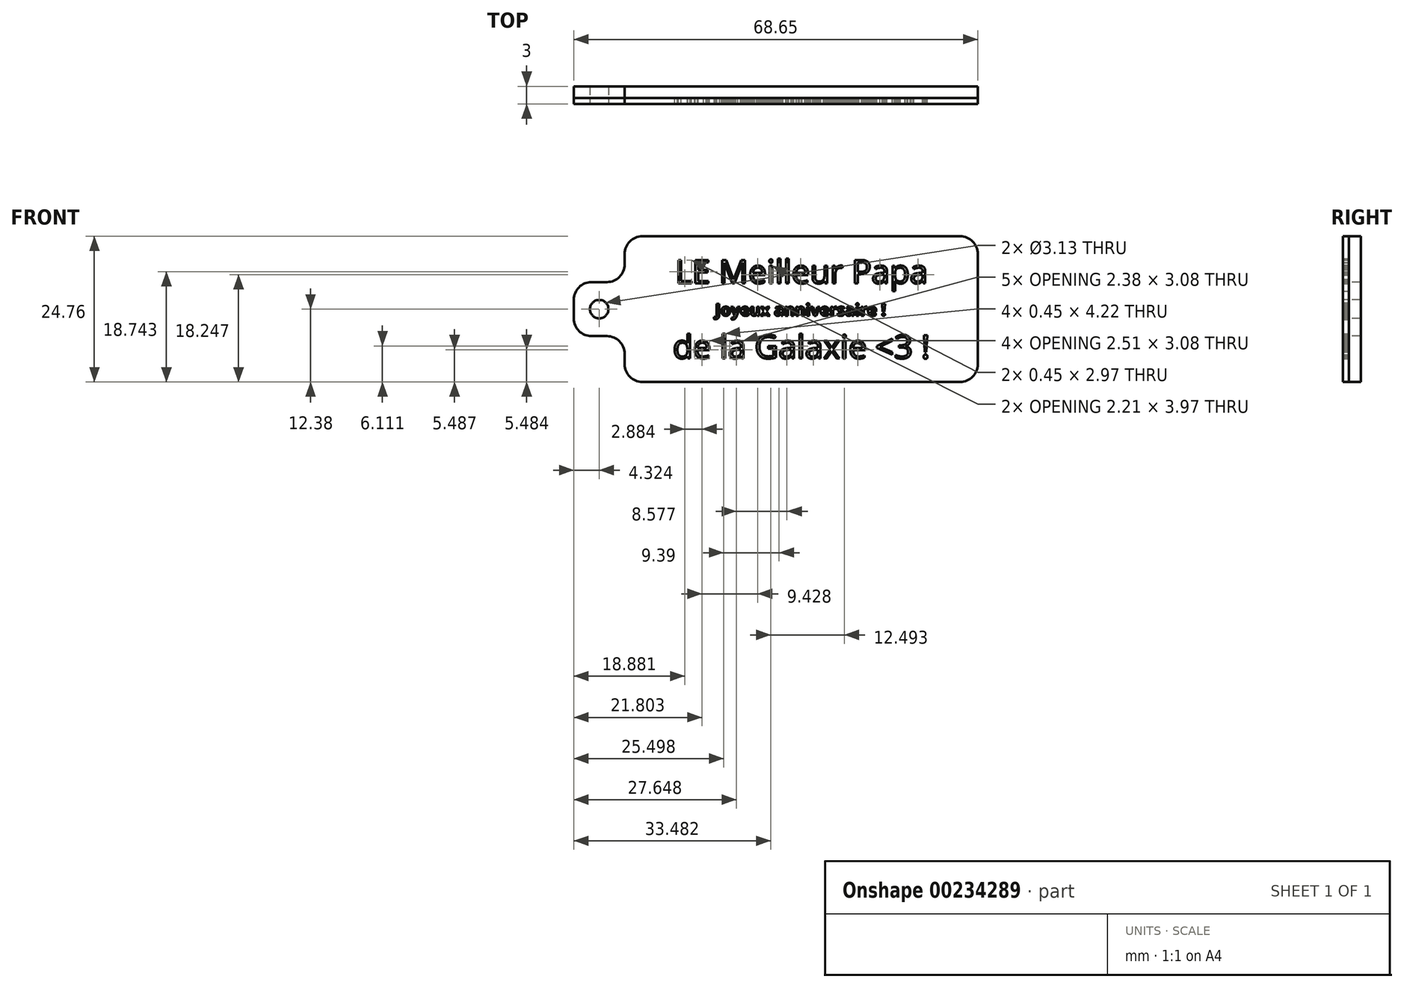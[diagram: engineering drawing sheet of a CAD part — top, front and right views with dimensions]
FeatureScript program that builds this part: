
annotation { "Feature Type Name" : "Feature", "Feature Type Description" : "" }
export const myFeature = defineFeature(function(context is Context, id is Id, definition is map)
    precondition{}
    {
        {
            var Q0;
            Q0=qCreatedBy(makeId("Front.planeOp"),FACE);
            var sketch = newSketch(context, id + "F0", { "sketchPlane" : qUnion([Q0])});
            skLineSegment(sketch, "E0.bottom", {"start": v(30, -12.38) * mm, "end": v(-30, -12.38) * mm});
            skLineSegment(sketch, "E0.top", {"start": v(30, 12.38) * mm, "end": v(-30, 12.38) * mm});
            skLineSegment(sketch, "E0.left", {"start": v(30, -12.38) * mm, "end": v(30, 12.38) * mm});
            skLineSegment(sketch, "E0.right", {"start": v(-30, -12.38) * mm, "end": v(-30, 12.38) * mm});
            skPoint(sketch, "E0.middle", {"position": v(0, 0) * mm});
            skText(sketch, "E1", { "text": "LE Meilleur Papa", "fontName": "OpenSans-Regular.ttf"});
            skLineSegment(sketch, "E2", {"start": v(0, 12.38) * mm, "end": v(0, 0) * mm, "construction": true});
            skText(sketch, "E3", { "text": "de la Galaxie <3 !", "fontName": "OpenSans-Regular.ttf"});
            skLineSegment(sketch, "E4.bottom", {"start": v(-30, -4.6) * mm, "end": v(-38.65, -4.6) * mm});
            skLineSegment(sketch, "E4.top", {"start": v(-30, 4.6) * mm, "end": v(-38.65, 4.6) * mm});
            skLineSegment(sketch, "E4.left", {"start": v(-30, -4.6) * mm, "end": v(-30, 4.6) * mm});
            skLineSegment(sketch, "E4.right", {"start": v(-38.65, -4.6) * mm, "end": v(-38.65, 4.6) * mm});
            skPoint(sketch, "E4.middle", {"position": v(-34.33, 0) * mm});
            skPoint(sketch, "E4.middle.positionSnap0", {"position": v(-30, 0) * mm});
            skPoint(sketch, "E4.centerSnap0", {"position": v(-30, 0) * mm});
            const initialGuessF0  = {"E1": [-0.02142, 0.00438, 1, 0, 0.004], "E3": [-0.02182, -0.00838, 1, 0, 0.004]};
            skSetInitialGuess(sketch, initialGuessF0);
            skSolve(sketch);
        }
        {
            var Q0;
            Q0 = qSketchRegion(id + "F0", true);
            var Q1;
            Q1=makeQuery(id+"F0.imprint","IMPRINT",FACE,{"disambiguationData":[TD([[makeQuery(id+"F0.imprint","IMPRINT",EDGE,{"derivedFrom":sQuery(id+"F0.wireOp",EDGE,"E1.sketch_text.stroke-50")}),1.0]])]});
            var Q2;
            Q2=makeQuery(id+"F0.imprint","IMPRINT",FACE,{"disambiguationData":[TD([[makeQuery(id+"F0.imprint","IMPRINT",EDGE,{"derivedFrom":sQuery(id+"F0.wireOp",EDGE,"E1.sketch_text.stroke-89")}),1.0]])]});
            var Q3;
            Q3=makeQuery(id+"F0.imprint","IMPRINT",FACE,{"disambiguationData":[TD([[makeQuery(id+"F0.imprint","IMPRINT",EDGE,{"derivedFrom":sQuery(id+"F0.wireOp",EDGE,"E1.sketch_text.stroke-132")}),1.0]])]});
            var Q4;
            Q4=makeQuery(id+"F0.imprint","IMPRINT",FACE,{"disambiguationData":[TD([[makeQuery(id+"F0.imprint","IMPRINT",EDGE,{"derivedFrom":sQuery(id+"F0.wireOp",EDGE,"E1.sketch_text.stroke-158")}),1.0]])]});
            var Q5;
            Q5=makeQuery(id+"F0.imprint","IMPRINT",FACE,{"disambiguationData":[TD([[makeQuery(id+"F0.imprint","IMPRINT",EDGE,{"derivedFrom":sQuery(id+"F0.wireOp",EDGE,"E1.sketch_text.stroke-182")}),1.0]])]});
            var Q6;
            Q6=makeQuery(id+"F0.imprint","IMPRINT",FACE,{"disambiguationData":[TD([[makeQuery(id+"F0.imprint","IMPRINT",EDGE,{"derivedFrom":sQuery(id+"F0.wireOp",EDGE,"E1.sketch_text.stroke-210")}),1.0]])]});
            var Q7;
            Q7=makeQuery(id+"F0.imprint","IMPRINT",FACE,{"disambiguationData":[TD([[makeQuery(id+"F0.imprint","IMPRINT",EDGE,{"derivedFrom":sQuery(id+"F0.wireOp",EDGE,"E3.sketch_text.stroke-15")}),1.0]])]});
            var Q8;
            Q8=makeQuery(id+"F0.imprint","IMPRINT",FACE,{"disambiguationData":[TD([[makeQuery(id+"F0.imprint","IMPRINT",EDGE,{"derivedFrom":sQuery(id+"F0.wireOp",EDGE,"E3.sketch_text.stroke-38")}),1.0]])]});
            var Q9;
            Q9=makeQuery(id+"F0.imprint","IMPRINT",FACE,{"disambiguationData":[TD([[makeQuery(id+"F0.imprint","IMPRINT",EDGE,{"derivedFrom":sQuery(id+"F0.wireOp",EDGE,"E3.sketch_text.stroke-66")}),1.0]])]});
            var Q10;
            Q10=makeQuery(id+"F0.imprint","IMPRINT",FACE,{"disambiguationData":[TD([[makeQuery(id+"F0.imprint","IMPRINT",EDGE,{"derivedFrom":sQuery(id+"F0.wireOp",EDGE,"E3.sketch_text.stroke-113")}),1.0]])]});
            var Q11;
            Q11=makeQuery(id+"F0.imprint","IMPRINT",FACE,{"disambiguationData":[TD([[makeQuery(id+"F0.imprint","IMPRINT",EDGE,{"derivedFrom":sQuery(id+"F0.wireOp",EDGE,"E3.sketch_text.stroke-144")}),1.0]])]});
            var Q12;
            Q12=makeQuery(id+"F0.imprint","IMPRINT",FACE,{"disambiguationData":[TD([[makeQuery(id+"F0.imprint","IMPRINT",EDGE,{"derivedFrom":sQuery(id+"F0.wireOp",EDGE,"E3.sketch_text.stroke-190")}),1.0]])]});
            extrude(context, id + "F1", {"entities" : qUnion([Q0, Q1, Q2, Q3, Q4, Q5, Q6, Q7, Q8, Q9, Q10, Q11, Q12]), "depth" : 1 * mm});
        }
        {
            var Q0;
            Q0=makeQuery(id+"F1.opExtrude","CAP_FACE",FACE,{"disambiguationData":[OSD([sQuery(id+"F0.wireOp",EDGE,"E0.bottom"),sQuery(id+"F0.wireOp",EDGE,"E0.top"),sQuery(id+"F0.wireOp",EDGE,"E0.left"),sQuery(id+"F0.wireOp",EDGE,"E0.right"),sQuery(id+"F0.wireOp",EDGE,"E1.sketch_text.stroke-0"),sQuery(id+"F0.wireOp",EDGE,"E1.sketch_text.stroke-1"),sQuery(id+"F0.wireOp",EDGE,"E1.sketch_text.stroke-2"),sQuery(id+"F0.wireOp",EDGE,"E1.sketch_text.stroke-3"),sQuery(id+"F0.wireOp",EDGE,"E1.sketch_text.stroke-4"),sQuery(id+"F0.wireOp",EDGE,"E1.sketch_text.stroke-5"),sQuery(id+"F0.wireOp",EDGE,"E1.sketch_text.stroke-6"),sQuery(id+"F0.wireOp",EDGE,"E1.sketch_text.stroke-7"),sQuery(id+"F0.wireOp",EDGE,"E1.sketch_text.stroke-8"),sQuery(id+"F0.wireOp",EDGE,"E1.sketch_text.stroke-9"),sQuery(id+"F0.wireOp",EDGE,"E1.sketch_text.stroke-10"),sQuery(id+"F0.wireOp",EDGE,"E1.sketch_text.stroke-11"),sQuery(id+"F0.wireOp",EDGE,"E1.sketch_text.stroke-12"),sQuery(id+"F0.wireOp",EDGE,"E1.sketch_text.stroke-13"),sQuery(id+"F0.wireOp",EDGE,"E1.sketch_text.stroke-14"),sQuery(id+"F0.wireOp",EDGE,"E1.sketch_text.stroke-15"),sQuery(id+"F0.wireOp",EDGE,"E1.sketch_text.stroke-16"),sQuery(id+"F0.wireOp",EDGE,"E1.sketch_text.stroke-17"),sQuery(id+"F0.wireOp",EDGE,"E1.sketch_text.stroke-18"),sQuery(id+"F0.wireOp",EDGE,"E1.sketch_text.stroke-19"),sQuery(id+"F0.wireOp",EDGE,"E1.sketch_text.stroke-20"),sQuery(id+"F0.wireOp",EDGE,"E1.sketch_text.stroke-21"),sQuery(id+"F0.wireOp",EDGE,"E1.sketch_text.stroke-22"),sQuery(id+"F0.wireOp",EDGE,"E1.sketch_text.stroke-23"),sQuery(id+"F0.wireOp",EDGE,"E1.sketch_text.stroke-24"),sQuery(id+"F0.wireOp",EDGE,"E1.sketch_text.stroke-25"),sQuery(id+"F0.wireOp",EDGE,"E1.sketch_text.stroke-26"),sQuery(id+"F0.wireOp",EDGE,"E1.sketch_text.stroke-27"),sQuery(id+"F0.wireOp",EDGE,"E1.sketch_text.stroke-28"),sQuery(id+"F0.wireOp",EDGE,"E1.sketch_text.stroke-29"),sQuery(id+"F0.wireOp",EDGE,"E1.sketch_text.stroke-30"),sQuery(id+"F0.wireOp",EDGE,"E1.sketch_text.stroke-31"),sQuery(id+"F0.wireOp",EDGE,"E1.sketch_text.stroke-32"),sQuery(id+"F0.wireOp",EDGE,"E1.sketch_text.stroke-33"),sQuery(id+"F0.wireOp",EDGE,"E1.sketch_text.stroke-34"),sQuery(id+"F0.wireOp",EDGE,"E1.sketch_text.stroke-35"),sQuery(id+"F0.wireOp",EDGE,"E1.sketch_text.stroke-36"),sQuery(id+"F0.wireOp",EDGE,"E1.sketch_text.stroke-37"),sQuery(id+"F0.wireOp",EDGE,"E1.sketch_text.stroke-38"),sQuery(id+"F0.wireOp",EDGE,"E1.sketch_text.stroke-39"),sQuery(id+"F0.wireOp",EDGE,"E1.sketch_text.stroke-40"),sQuery(id+"F0.wireOp",EDGE,"E1.sketch_text.stroke-41"),sQuery(id+"F0.wireOp",EDGE,"E1.sketch_text.stroke-42"),sQuery(id+"F0.wireOp",EDGE,"E1.sketch_text.stroke-43"),sQuery(id+"F0.wireOp",EDGE,"E1.sketch_text.stroke-44"),sQuery(id+"F0.wireOp",EDGE,"E1.sketch_text.stroke-45"),sQuery(id+"F0.wireOp",EDGE,"E1.sketch_text.stroke-46"),sQuery(id+"F0.wireOp",EDGE,"E1.sketch_text.stroke-47"),sQuery(id+"F0.wireOp",EDGE,"E1.sketch_text.stroke-48"),sQuery(id+"F0.wireOp",EDGE,"E1.sketch_text.stroke-49"),sQuery(id+"F0.wireOp",EDGE,"E1.sketch_text.stroke-55"),sQuery(id+"F0.wireOp",EDGE,"E1.sketch_text.stroke-56"),sQuery(id+"F0.wireOp",EDGE,"E1.sketch_text.stroke-57"),sQuery(id+"F0.wireOp",EDGE,"E1.sketch_text.stroke-58"),sQuery(id+"F0.wireOp",EDGE,"E1.sketch_text.stroke-59"),sQuery(id+"F0.wireOp",EDGE,"E1.sketch_text.stroke-60"),sQuery(id+"F0.wireOp",EDGE,"E1.sketch_text.stroke-61"),sQuery(id+"F0.wireOp",EDGE,"E1.sketch_text.stroke-62"),sQuery(id+"F0.wireOp",EDGE,"E1.sketch_text.stroke-63"),sQuery(id+"F0.wireOp",EDGE,"E1.sketch_text.stroke-64"),sQuery(id+"F0.wireOp",EDGE,"E1.sketch_text.stroke-65"),sQuery(id+"F0.wireOp",EDGE,"E1.sketch_text.stroke-66"),sQuery(id+"F0.wireOp",EDGE,"E1.sketch_text.stroke-67"),sQuery(id+"F0.wireOp",EDGE,"E1.sketch_text.stroke-68"),sQuery(id+"F0.wireOp",EDGE,"E1.sketch_text.stroke-69"),sQuery(id+"F0.wireOp",EDGE,"E1.sketch_text.stroke-70"),sQuery(id+"F0.wireOp",EDGE,"E1.sketch_text.stroke-71"),sQuery(id+"F0.wireOp",EDGE,"E1.sketch_text.stroke-72"),sQuery(id+"F0.wireOp",EDGE,"E1.sketch_text.stroke-73"),sQuery(id+"F0.wireOp",EDGE,"E1.sketch_text.stroke-74"),sQuery(id+"F0.wireOp",EDGE,"E1.sketch_text.stroke-75"),sQuery(id+"F0.wireOp",EDGE,"E1.sketch_text.stroke-76"),sQuery(id+"F0.wireOp",EDGE,"E1.sketch_text.stroke-77"),sQuery(id+"F0.wireOp",EDGE,"E1.sketch_text.stroke-78"),sQuery(id+"F0.wireOp",EDGE,"E1.sketch_text.stroke-79"),sQuery(id+"F0.wireOp",EDGE,"E1.sketch_text.stroke-80"),sQuery(id+"F0.wireOp",EDGE,"E1.sketch_text.stroke-81"),sQuery(id+"F0.wireOp",EDGE,"E1.sketch_text.stroke-82"),sQuery(id+"F0.wireOp",EDGE,"E1.sketch_text.stroke-83"),sQuery(id+"F0.wireOp",EDGE,"E1.sketch_text.stroke-84"),sQuery(id+"F0.wireOp",EDGE,"E1.sketch_text.stroke-85"),sQuery(id+"F0.wireOp",EDGE,"E1.sketch_text.stroke-86"),sQuery(id+"F0.wireOp",EDGE,"E1.sketch_text.stroke-87"),sQuery(id+"F0.wireOp",EDGE,"E1.sketch_text.stroke-88"),sQuery(id+"F0.wireOp",EDGE,"E1.sketch_text.stroke-94"),sQuery(id+"F0.wireOp",EDGE,"E1.sketch_text.stroke-95"),sQuery(id+"F0.wireOp",EDGE,"E1.sketch_text.stroke-96"),sQuery(id+"F0.wireOp",EDGE,"E1.sketch_text.stroke-97"),sQuery(id+"F0.wireOp",EDGE,"E1.sketch_text.stroke-98"),sQuery(id+"F0.wireOp",EDGE,"E1.sketch_text.stroke-99"),sQuery(id+"F0.wireOp",EDGE,"E1.sketch_text.stroke-100"),sQuery(id+"F0.wireOp",EDGE,"E1.sketch_text.stroke-101"),sQuery(id+"F0.wireOp",EDGE,"E1.sketch_text.stroke-102"),sQuery(id+"F0.wireOp",EDGE,"E1.sketch_text.stroke-103"),sQuery(id+"F0.wireOp",EDGE,"E1.sketch_text.stroke-104"),sQuery(id+"F0.wireOp",EDGE,"E1.sketch_text.stroke-105"),sQuery(id+"F0.wireOp",EDGE,"E1.sketch_text.stroke-106"),sQuery(id+"F0.wireOp",EDGE,"E1.sketch_text.stroke-107"),sQuery(id+"F0.wireOp",EDGE,"E1.sketch_text.stroke-108"),sQuery(id+"F0.wireOp",EDGE,"E1.sketch_text.stroke-109"),sQuery(id+"F0.wireOp",EDGE,"E1.sketch_text.stroke-110"),sQuery(id+"F0.wireOp",EDGE,"E1.sketch_text.stroke-111"),sQuery(id+"F0.wireOp",EDGE,"E1.sketch_text.stroke-112"),sQuery(id+"F0.wireOp",EDGE,"E1.sketch_text.stroke-113"),sQuery(id+"F0.wireOp",EDGE,"E1.sketch_text.stroke-114"),sQuery(id+"F0.wireOp",EDGE,"E1.sketch_text.stroke-115"),sQuery(id+"F0.wireOp",EDGE,"E1.sketch_text.stroke-116"),sQuery(id+"F0.wireOp",EDGE,"E1.sketch_text.stroke-117"),sQuery(id+"F0.wireOp",EDGE,"E1.sketch_text.stroke-118"),sQuery(id+"F0.wireOp",EDGE,"E1.sketch_text.stroke-119"),sQuery(id+"F0.wireOp",EDGE,"E1.sketch_text.stroke-120"),sQuery(id+"F0.wireOp",EDGE,"E1.sketch_text.stroke-121"),sQuery(id+"F0.wireOp",EDGE,"E1.sketch_text.stroke-122"),sQuery(id+"F0.wireOp",EDGE,"E1.sketch_text.stroke-123"),sQuery(id+"F0.wireOp",EDGE,"E1.sketch_text.stroke-124"),sQuery(id+"F0.wireOp",EDGE,"E1.sketch_text.stroke-125"),sQuery(id+"F0.wireOp",EDGE,"E1.sketch_text.stroke-126"),sQuery(id+"F0.wireOp",EDGE,"E1.sketch_text.stroke-127"),sQuery(id+"F0.wireOp",EDGE,"E1.sketch_text.stroke-128"),sQuery(id+"F0.wireOp",EDGE,"E1.sketch_text.stroke-129"),sQuery(id+"F0.wireOp",EDGE,"E1.sketch_text.stroke-130"),sQuery(id+"F0.wireOp",EDGE,"E1.sketch_text.stroke-131"),sQuery(id+"F0.wireOp",EDGE,"E1.sketch_text.stroke-139"),sQuery(id+"F0.wireOp",EDGE,"E1.sketch_text.stroke-140"),sQuery(id+"F0.wireOp",EDGE,"E1.sketch_text.stroke-141"),sQuery(id+"F0.wireOp",EDGE,"E1.sketch_text.stroke-142"),sQuery(id+"F0.wireOp",EDGE,"E1.sketch_text.stroke-143"),sQuery(id+"F0.wireOp",EDGE,"E1.sketch_text.stroke-144"),sQuery(id+"F0.wireOp",EDGE,"E1.sketch_text.stroke-145"),sQuery(id+"F0.wireOp",EDGE,"E1.sketch_text.stroke-146"),sQuery(id+"F0.wireOp",EDGE,"E1.sketch_text.stroke-147"),sQuery(id+"F0.wireOp",EDGE,"E1.sketch_text.stroke-148"),sQuery(id+"F0.wireOp",EDGE,"E1.sketch_text.stroke-149"),sQuery(id+"F0.wireOp",EDGE,"E1.sketch_text.stroke-150"),sQuery(id+"F0.wireOp",EDGE,"E1.sketch_text.stroke-151"),sQuery(id+"F0.wireOp",EDGE,"E1.sketch_text.stroke-152"),sQuery(id+"F0.wireOp",EDGE,"E1.sketch_text.stroke-153"),sQuery(id+"F0.wireOp",EDGE,"E1.sketch_text.stroke-154"),sQuery(id+"F0.wireOp",EDGE,"E1.sketch_text.stroke-155"),sQuery(id+"F0.wireOp",EDGE,"E1.sketch_text.stroke-156"),sQuery(id+"F0.wireOp",EDGE,"E1.sketch_text.stroke-157"),sQuery(id+"F0.wireOp",EDGE,"E1.sketch_text.stroke-166"),sQuery(id+"F0.wireOp",EDGE,"E1.sketch_text.stroke-167"),sQuery(id+"F0.wireOp",EDGE,"E1.sketch_text.stroke-168"),sQuery(id+"F0.wireOp",EDGE,"E1.sketch_text.stroke-169"),sQuery(id+"F0.wireOp",EDGE,"E1.sketch_text.stroke-170"),sQuery(id+"F0.wireOp",EDGE,"E1.sketch_text.stroke-171"),sQuery(id+"F0.wireOp",EDGE,"E1.sketch_text.stroke-172"),sQuery(id+"F0.wireOp",EDGE,"E1.sketch_text.stroke-173"),sQuery(id+"F0.wireOp",EDGE,"E1.sketch_text.stroke-174"),sQuery(id+"F0.wireOp",EDGE,"E1.sketch_text.stroke-175"),sQuery(id+"F0.wireOp",EDGE,"E1.sketch_text.stroke-176"),sQuery(id+"F0.wireOp",EDGE,"E1.sketch_text.stroke-177"),sQuery(id+"F0.wireOp",EDGE,"E1.sketch_text.stroke-178"),sQuery(id+"F0.wireOp",EDGE,"E1.sketch_text.stroke-179"),sQuery(id+"F0.wireOp",EDGE,"E1.sketch_text.stroke-180"),sQuery(id+"F0.wireOp",EDGE,"E1.sketch_text.stroke-181"),sQuery(id+"F0.wireOp",EDGE,"E1.sketch_text.stroke-191"),sQuery(id+"F0.wireOp",EDGE,"E1.sketch_text.stroke-192"),sQuery(id+"F0.wireOp",EDGE,"E1.sketch_text.stroke-193"),sQuery(id+"F0.wireOp",EDGE,"E1.sketch_text.stroke-194"),sQuery(id+"F0.wireOp",EDGE,"E1.sketch_text.stroke-195"),sQuery(id+"F0.wireOp",EDGE,"E1.sketch_text.stroke-196"),sQuery(id+"F0.wireOp",EDGE,"E1.sketch_text.stroke-197"),sQuery(id+"F0.wireOp",EDGE,"E1.sketch_text.stroke-198"),sQuery(id+"F0.wireOp",EDGE,"E1.sketch_text.stroke-199"),sQuery(id+"F0.wireOp",EDGE,"E1.sketch_text.stroke-200"),sQuery(id+"F0.wireOp",EDGE,"E1.sketch_text.stroke-201"),sQuery(id+"F0.wireOp",EDGE,"E1.sketch_text.stroke-202"),sQuery(id+"F0.wireOp",EDGE,"E1.sketch_text.stroke-203"),sQuery(id+"F0.wireOp",EDGE,"E1.sketch_text.stroke-204"),sQuery(id+"F0.wireOp",EDGE,"E1.sketch_text.stroke-205"),sQuery(id+"F0.wireOp",EDGE,"E1.sketch_text.stroke-206"),sQuery(id+"F0.wireOp",EDGE,"E1.sketch_text.stroke-207"),sQuery(id+"F0.wireOp",EDGE,"E1.sketch_text.stroke-208"),sQuery(id+"F0.wireOp",EDGE,"E1.sketch_text.stroke-209"),sQuery(id+"F0.wireOp",EDGE,"E3.sketch_text.stroke-0"),sQuery(id+"F0.wireOp",EDGE,"E3.sketch_text.stroke-1"),sQuery(id+"F0.wireOp",EDGE,"E3.sketch_text.stroke-2"),sQuery(id+"F0.wireOp",EDGE,"E3.sketch_text.stroke-3"),sQuery(id+"F0.wireOp",EDGE,"E3.sketch_text.stroke-4"),sQuery(id+"F0.wireOp",EDGE,"E3.sketch_text.stroke-5"),sQuery(id+"F0.wireOp",EDGE,"E3.sketch_text.stroke-6"),sQuery(id+"F0.wireOp",EDGE,"E3.sketch_text.stroke-7"),sQuery(id+"F0.wireOp",EDGE,"E3.sketch_text.stroke-8"),sQuery(id+"F0.wireOp",EDGE,"E3.sketch_text.stroke-9"),sQuery(id+"F0.wireOp",EDGE,"E3.sketch_text.stroke-10"),sQuery(id+"F0.wireOp",EDGE,"E3.sketch_text.stroke-11"),sQuery(id+"F0.wireOp",EDGE,"E3.sketch_text.stroke-12"),sQuery(id+"F0.wireOp",EDGE,"E3.sketch_text.stroke-13"),sQuery(id+"F0.wireOp",EDGE,"E3.sketch_text.stroke-14"),sQuery(id+"F0.wireOp",EDGE,"E3.sketch_text.stroke-24"),sQuery(id+"F0.wireOp",EDGE,"E3.sketch_text.stroke-25"),sQuery(id+"F0.wireOp",EDGE,"E3.sketch_text.stroke-26"),sQuery(id+"F0.wireOp",EDGE,"E3.sketch_text.stroke-27"),sQuery(id+"F0.wireOp",EDGE,"E3.sketch_text.stroke-28"),sQuery(id+"F0.wireOp",EDGE,"E3.sketch_text.stroke-29"),sQuery(id+"F0.wireOp",EDGE,"E3.sketch_text.stroke-30"),sQuery(id+"F0.wireOp",EDGE,"E3.sketch_text.stroke-31"),sQuery(id+"F0.wireOp",EDGE,"E3.sketch_text.stroke-32"),sQuery(id+"F0.wireOp",EDGE,"E3.sketch_text.stroke-33"),sQuery(id+"F0.wireOp",EDGE,"E3.sketch_text.stroke-34"),sQuery(id+"F0.wireOp",EDGE,"E3.sketch_text.stroke-35"),sQuery(id+"F0.wireOp",EDGE,"E3.sketch_text.stroke-36"),sQuery(id+"F0.wireOp",EDGE,"E3.sketch_text.stroke-37"),sQuery(id+"F0.wireOp",EDGE,"E3.sketch_text.stroke-43"),sQuery(id+"F0.wireOp",EDGE,"E3.sketch_text.stroke-44"),sQuery(id+"F0.wireOp",EDGE,"E3.sketch_text.stroke-45"),sQuery(id+"F0.wireOp",EDGE,"E3.sketch_text.stroke-46"),sQuery(id+"F0.wireOp",EDGE,"E3.sketch_text.stroke-47"),sQuery(id+"F0.wireOp",EDGE,"E3.sketch_text.stroke-48"),sQuery(id+"F0.wireOp",EDGE,"E3.sketch_text.stroke-49"),sQuery(id+"F0.wireOp",EDGE,"E3.sketch_text.stroke-50"),sQuery(id+"F0.wireOp",EDGE,"E3.sketch_text.stroke-51"),sQuery(id+"F0.wireOp",EDGE,"E3.sketch_text.stroke-52"),sQuery(id+"F0.wireOp",EDGE,"E3.sketch_text.stroke-53"),sQuery(id+"F0.wireOp",EDGE,"E3.sketch_text.stroke-54"),sQuery(id+"F0.wireOp",EDGE,"E3.sketch_text.stroke-55"),sQuery(id+"F0.wireOp",EDGE,"E3.sketch_text.stroke-56"),sQuery(id+"F0.wireOp",EDGE,"E3.sketch_text.stroke-57"),sQuery(id+"F0.wireOp",EDGE,"E3.sketch_text.stroke-58"),sQuery(id+"F0.wireOp",EDGE,"E3.sketch_text.stroke-59"),sQuery(id+"F0.wireOp",EDGE,"E3.sketch_text.stroke-60"),sQuery(id+"F0.wireOp",EDGE,"E3.sketch_text.stroke-61"),sQuery(id+"F0.wireOp",EDGE,"E3.sketch_text.stroke-62"),sQuery(id+"F0.wireOp",EDGE,"E3.sketch_text.stroke-63"),sQuery(id+"F0.wireOp",EDGE,"E3.sketch_text.stroke-64"),sQuery(id+"F0.wireOp",EDGE,"E3.sketch_text.stroke-65"),sQuery(id+"F0.wireOp",EDGE,"E3.sketch_text.stroke-74"),sQuery(id+"F0.wireOp",EDGE,"E3.sketch_text.stroke-75"),sQuery(id+"F0.wireOp",EDGE,"E3.sketch_text.stroke-76"),sQuery(id+"F0.wireOp",EDGE,"E3.sketch_text.stroke-77"),sQuery(id+"F0.wireOp",EDGE,"E3.sketch_text.stroke-78"),sQuery(id+"F0.wireOp",EDGE,"E3.sketch_text.stroke-79"),sQuery(id+"F0.wireOp",EDGE,"E3.sketch_text.stroke-80"),sQuery(id+"F0.wireOp",EDGE,"E3.sketch_text.stroke-81"),sQuery(id+"F0.wireOp",EDGE,"E3.sketch_text.stroke-82"),sQuery(id+"F0.wireOp",EDGE,"E3.sketch_text.stroke-83"),sQuery(id+"F0.wireOp",EDGE,"E3.sketch_text.stroke-84"),sQuery(id+"F0.wireOp",EDGE,"E3.sketch_text.stroke-85"),sQuery(id+"F0.wireOp",EDGE,"E3.sketch_text.stroke-86"),sQuery(id+"F0.wireOp",EDGE,"E3.sketch_text.stroke-87"),sQuery(id+"F0.wireOp",EDGE,"E3.sketch_text.stroke-88"),sQuery(id+"F0.wireOp",EDGE,"E3.sketch_text.stroke-89"),sQuery(id+"F0.wireOp",EDGE,"E3.sketch_text.stroke-90"),sQuery(id+"F0.wireOp",EDGE,"E3.sketch_text.stroke-91"),sQuery(id+"F0.wireOp",EDGE,"E3.sketch_text.stroke-92"),sQuery(id+"F0.wireOp",EDGE,"E3.sketch_text.stroke-93"),sQuery(id+"F0.wireOp",EDGE,"E3.sketch_text.stroke-94"),sQuery(id+"F0.wireOp",EDGE,"E3.sketch_text.stroke-95"),sQuery(id+"F0.wireOp",EDGE,"E3.sketch_text.stroke-96"),sQuery(id+"F0.wireOp",EDGE,"E3.sketch_text.stroke-97"),sQuery(id+"F0.wireOp",EDGE,"E3.sketch_text.stroke-98"),sQuery(id+"F0.wireOp",EDGE,"E3.sketch_text.stroke-99"),sQuery(id+"F0.wireOp",EDGE,"E3.sketch_text.stroke-100"),sQuery(id+"F0.wireOp",EDGE,"E3.sketch_text.stroke-101"),sQuery(id+"F0.wireOp",EDGE,"E3.sketch_text.stroke-102"),sQuery(id+"F0.wireOp",EDGE,"E3.sketch_text.stroke-103"),sQuery(id+"F0.wireOp",EDGE,"E3.sketch_text.stroke-104"),sQuery(id+"F0.wireOp",EDGE,"E3.sketch_text.stroke-105"),sQuery(id+"F0.wireOp",EDGE,"E3.sketch_text.stroke-106"),sQuery(id+"F0.wireOp",EDGE,"E3.sketch_text.stroke-107"),sQuery(id+"F0.wireOp",EDGE,"E3.sketch_text.stroke-108"),sQuery(id+"F0.wireOp",EDGE,"E3.sketch_text.stroke-109"),sQuery(id+"F0.wireOp",EDGE,"E3.sketch_text.stroke-110"),sQuery(id+"F0.wireOp",EDGE,"E3.sketch_text.stroke-111"),sQuery(id+"F0.wireOp",EDGE,"E3.sketch_text.stroke-112"),sQuery(id+"F0.wireOp",EDGE,"E3.sketch_text.stroke-121"),sQuery(id+"F0.wireOp",EDGE,"E3.sketch_text.stroke-122"),sQuery(id+"F0.wireOp",EDGE,"E3.sketch_text.stroke-123"),sQuery(id+"F0.wireOp",EDGE,"E3.sketch_text.stroke-124"),sQuery(id+"F0.wireOp",EDGE,"E3.sketch_text.stroke-125"),sQuery(id+"F0.wireOp",EDGE,"E3.sketch_text.stroke-126"),sQuery(id+"F0.wireOp",EDGE,"E3.sketch_text.stroke-127"),sQuery(id+"F0.wireOp",EDGE,"E3.sketch_text.stroke-128"),sQuery(id+"F0.wireOp",EDGE,"E3.sketch_text.stroke-129"),sQuery(id+"F0.wireOp",EDGE,"E3.sketch_text.stroke-130"),sQuery(id+"F0.wireOp",EDGE,"E3.sketch_text.stroke-131"),sQuery(id+"F0.wireOp",EDGE,"E3.sketch_text.stroke-132"),sQuery(id+"F0.wireOp",EDGE,"E3.sketch_text.stroke-133"),sQuery(id+"F0.wireOp",EDGE,"E3.sketch_text.stroke-134"),sQuery(id+"F0.wireOp",EDGE,"E3.sketch_text.stroke-135"),sQuery(id+"F0.wireOp",EDGE,"E3.sketch_text.stroke-136"),sQuery(id+"F0.wireOp",EDGE,"E3.sketch_text.stroke-137"),sQuery(id+"F0.wireOp",EDGE,"E3.sketch_text.stroke-138"),sQuery(id+"F0.wireOp",EDGE,"E3.sketch_text.stroke-139"),sQuery(id+"F0.wireOp",EDGE,"E3.sketch_text.stroke-140"),sQuery(id+"F0.wireOp",EDGE,"E3.sketch_text.stroke-141"),sQuery(id+"F0.wireOp",EDGE,"E3.sketch_text.stroke-142"),sQuery(id+"F0.wireOp",EDGE,"E3.sketch_text.stroke-143"),sQuery(id+"F0.wireOp",EDGE,"E3.sketch_text.stroke-152"),sQuery(id+"F0.wireOp",EDGE,"E3.sketch_text.stroke-153"),sQuery(id+"F0.wireOp",EDGE,"E3.sketch_text.stroke-154"),sQuery(id+"F0.wireOp",EDGE,"E3.sketch_text.stroke-155"),sQuery(id+"F0.wireOp",EDGE,"E3.sketch_text.stroke-156"),sQuery(id+"F0.wireOp",EDGE,"E3.sketch_text.stroke-157"),sQuery(id+"F0.wireOp",EDGE,"E3.sketch_text.stroke-158"),sQuery(id+"F0.wireOp",EDGE,"E3.sketch_text.stroke-159"),sQuery(id+"F0.wireOp",EDGE,"E3.sketch_text.stroke-160"),sQuery(id+"F0.wireOp",EDGE,"E3.sketch_text.stroke-161"),sQuery(id+"F0.wireOp",EDGE,"E3.sketch_text.stroke-162"),sQuery(id+"F0.wireOp",EDGE,"E3.sketch_text.stroke-163"),sQuery(id+"F0.wireOp",EDGE,"E3.sketch_text.stroke-164"),sQuery(id+"F0.wireOp",EDGE,"E3.sketch_text.stroke-165"),sQuery(id+"F0.wireOp",EDGE,"E3.sketch_text.stroke-166"),sQuery(id+"F0.wireOp",EDGE,"E3.sketch_text.stroke-167"),sQuery(id+"F0.wireOp",EDGE,"E3.sketch_text.stroke-168"),sQuery(id+"F0.wireOp",EDGE,"E3.sketch_text.stroke-169"),sQuery(id+"F0.wireOp",EDGE,"E3.sketch_text.stroke-170"),sQuery(id+"F0.wireOp",EDGE,"E3.sketch_text.stroke-171"),sQuery(id+"F0.wireOp",EDGE,"E3.sketch_text.stroke-172"),sQuery(id+"F0.wireOp",EDGE,"E3.sketch_text.stroke-173"),sQuery(id+"F0.wireOp",EDGE,"E3.sketch_text.stroke-174"),sQuery(id+"F0.wireOp",EDGE,"E3.sketch_text.stroke-175"),sQuery(id+"F0.wireOp",EDGE,"E3.sketch_text.stroke-176"),sQuery(id+"F0.wireOp",EDGE,"E3.sketch_text.stroke-177"),sQuery(id+"F0.wireOp",EDGE,"E3.sketch_text.stroke-178"),sQuery(id+"F0.wireOp",EDGE,"E3.sketch_text.stroke-179"),sQuery(id+"F0.wireOp",EDGE,"E3.sketch_text.stroke-180"),sQuery(id+"F0.wireOp",EDGE,"E3.sketch_text.stroke-181"),sQuery(id+"F0.wireOp",EDGE,"E3.sketch_text.stroke-182"),sQuery(id+"F0.wireOp",EDGE,"E3.sketch_text.stroke-183"),sQuery(id+"F0.wireOp",EDGE,"E3.sketch_text.stroke-184"),sQuery(id+"F0.wireOp",EDGE,"E3.sketch_text.stroke-185"),sQuery(id+"F0.wireOp",EDGE,"E3.sketch_text.stroke-186"),sQuery(id+"F0.wireOp",EDGE,"E3.sketch_text.stroke-187"),sQuery(id+"F0.wireOp",EDGE,"E3.sketch_text.stroke-188"),sQuery(id+"F0.wireOp",EDGE,"E3.sketch_text.stroke-189"),sQuery(id+"F0.wireOp",EDGE,"E3.sketch_text.stroke-195"),sQuery(id+"F0.wireOp",EDGE,"E3.sketch_text.stroke-196"),sQuery(id+"F0.wireOp",EDGE,"E3.sketch_text.stroke-197"),sQuery(id+"F0.wireOp",EDGE,"E3.sketch_text.stroke-198"),sQuery(id+"F0.wireOp",EDGE,"E3.sketch_text.stroke-199"),sQuery(id+"F0.wireOp",EDGE,"E3.sketch_text.stroke-200"),sQuery(id+"F0.wireOp",EDGE,"E3.sketch_text.stroke-201"),sQuery(id+"F0.wireOp",EDGE,"E3.sketch_text.stroke-202"),sQuery(id+"F0.wireOp",EDGE,"E3.sketch_text.stroke-203"),sQuery(id+"F0.wireOp",EDGE,"E3.sketch_text.stroke-204"),sQuery(id+"F0.wireOp",EDGE,"E3.sketch_text.stroke-205"),sQuery(id+"F0.wireOp",EDGE,"E3.sketch_text.stroke-206"),sQuery(id+"F0.wireOp",EDGE,"E3.sketch_text.stroke-207"),sQuery(id+"F0.wireOp",EDGE,"E3.sketch_text.stroke-208"),sQuery(id+"F0.wireOp",EDGE,"E3.sketch_text.stroke-209"),sQuery(id+"F0.wireOp",EDGE,"E3.sketch_text.stroke-210"),sQuery(id+"F0.wireOp",EDGE,"E3.sketch_text.stroke-211"),sQuery(id+"F0.wireOp",EDGE,"E3.sketch_text.stroke-212"),sQuery(id+"F0.wireOp",EDGE,"E3.sketch_text.stroke-213"),sQuery(id+"F0.wireOp",EDGE,"E3.sketch_text.stroke-214"),sQuery(id+"F0.wireOp",EDGE,"E3.sketch_text.stroke-215"),sQuery(id+"F0.wireOp",EDGE,"E3.sketch_text.stroke-216"),sQuery(id+"F0.wireOp",EDGE,"E3.sketch_text.stroke-217"),sQuery(id+"F0.wireOp",EDGE,"E3.sketch_text.stroke-218"),sQuery(id+"F0.wireOp",EDGE,"E3.sketch_text.stroke-219"),sQuery(id+"F0.wireOp",EDGE,"E3.sketch_text.stroke-220"),sQuery(id+"F0.wireOp",EDGE,"E3.sketch_text.stroke-221"),sQuery(id+"F0.wireOp",EDGE,"E3.sketch_text.stroke-222"),sQuery(id+"F0.wireOp",EDGE,"E3.sketch_text.stroke-223"),sQuery(id+"F0.wireOp",EDGE,"E3.sketch_text.stroke-224"),sQuery(id+"F0.wireOp",EDGE,"E3.sketch_text.stroke-225"),sQuery(id+"F0.wireOp",EDGE,"E3.sketch_text.stroke-226"),sQuery(id+"F0.wireOp",EDGE,"E3.sketch_text.stroke-227"),sQuery(id+"F0.wireOp",EDGE,"E3.sketch_text.stroke-228"),sQuery(id+"F0.wireOp",EDGE,"E3.sketch_text.stroke-229"),sQuery(id+"F0.wireOp",EDGE,"E3.sketch_text.stroke-230"),sQuery(id+"F0.wireOp",EDGE,"E3.sketch_text.stroke-231"),sQuery(id+"F0.wireOp",EDGE,"E3.sketch_text.stroke-232"),sQuery(id+"F0.wireOp",EDGE,"E3.sketch_text.stroke-233"),sQuery(id+"F0.wireOp",EDGE,"E3.sketch_text.stroke-234"),sQuery(id+"F0.wireOp",EDGE,"E3.sketch_text.stroke-235"),sQuery(id+"F0.wireOp",EDGE,"E3.sketch_text.stroke-236"),sQuery(id+"F0.wireOp",EDGE,"E3.sketch_text.stroke-237"),sQuery(id+"F0.wireOp",EDGE,"E3.sketch_text.stroke-238"),sQuery(id+"F0.wireOp",EDGE,"E3.sketch_text.stroke-239"),sQuery(id+"F0.wireOp",EDGE,"E3.sketch_text.stroke-240")])],"isStart":true});
            var sketch = newSketch(context, id + "F2", { "sketchPlane" : qUnion([Q0])});
            skLineSegment(sketch, "E5.bottom", {"start": v(-30, 12.38) * mm, "end": v(30, 12.38) * mm});
            skLineSegment(sketch, "E5.top", {"start": v(-30, -12.38) * mm, "end": v(30, -12.38) * mm});
            skLineSegment(sketch, "E5.left", {"start": v(-30, 12.38) * mm, "end": v(-30, -12.38) * mm});
            skLineSegment(sketch, "E5.right", {"start": v(30, 12.38) * mm, "end": v(30, -12.38) * mm});
            skLineSegment(sketch, "E6.bottom", {"start": v(30, 4.6) * mm, "end": v(38.65, 4.6) * mm});
            skLineSegment(sketch, "E6.top", {"start": v(30, -4.6) * mm, "end": v(38.65, -4.6) * mm});
            skLineSegment(sketch, "E6.left", {"start": v(30, 4.6) * mm, "end": v(30, -4.6) * mm});
            skLineSegment(sketch, "E6.right", {"start": v(38.65, 4.6) * mm, "end": v(38.65, -4.6) * mm});
            skSolve(sketch);
        }
        {
            var Q0;
            Q0 = qSketchRegion(id + "F2", true);
            extrude(context, id + "F3", {"entities" : qUnion([Q0]), "depth" : 2 * mm});
        }
        {
            var Q0;
            Q0=makeQuery(id+"F3.opExtrude","SWEPT_EDGE",EDGE,{"disambiguationData":[OSD([sQuery(id+"F2.wireOp",EDGE,"E5.bottom"),sQuery(id+"F2.wireOp",EDGE,"E5.right")])]});
            var Q1;
            Q1=makeQuery(id+"F1.opExtrude","SWEPT_EDGE",EDGE,{"disambiguationData":[OSD([sQuery(id+"F0.wireOp",EDGE,"E0.top"),sQuery(id+"F0.wireOp",EDGE,"E0.right")])]});
            var Q2;
            Q2=makeQuery(id+"F3.opExtrude","SWEPT_EDGE",EDGE,{"disambiguationData":[OSD([sQuery(id+"F2.wireOp",EDGE,"E5.bottom"),sQuery(id+"F2.wireOp",EDGE,"E5.left")])]});
            var Q3;
            Q3=makeQuery(id+"F1.opExtrude","SWEPT_EDGE",EDGE,{"disambiguationData":[OSD([sQuery(id+"F0.wireOp",EDGE,"E0.top"),sQuery(id+"F0.wireOp",EDGE,"E0.left")])]});
            var Q4;
            Q4=makeQuery(id+"F3.opExtrude","SWEPT_EDGE",EDGE,{"disambiguationData":[OSD([sQuery(id+"F2.wireOp",EDGE,"E5.top"),sQuery(id+"F2.wireOp",EDGE,"E5.left")])]});
            var Q5;
            Q5=makeQuery(id+"F1.opExtrude","SWEPT_EDGE",EDGE,{"disambiguationData":[OSD([sQuery(id+"F0.wireOp",EDGE,"E0.bottom"),sQuery(id+"F0.wireOp",EDGE,"E0.left")])]});
            var Q6;
            Q6=makeQuery(id+"F3.opExtrude","SWEPT_EDGE",EDGE,{"disambiguationData":[OSD([sQuery(id+"F2.wireOp",EDGE,"E5.top"),sQuery(id+"F2.wireOp",EDGE,"E5.right")])]});
            var Q7;
            Q7=makeQuery(id+"F1.opExtrude","SWEPT_EDGE",EDGE,{"disambiguationData":[OSD([sQuery(id+"F0.wireOp",EDGE,"E0.bottom"),sQuery(id+"F0.wireOp",EDGE,"E0.right")])]});
            var Q8;
            Q8=makeQuery(id+"F3.opExtrude","SWEPT_EDGE",EDGE,{"disambiguationData":[OSD([sQuery(id+"F2.wireOp",EDGE,"E6.bottom"),sQuery(id+"F2.wireOp",EDGE,"E6.right")])]});
            var Q9;
            Q9=makeQuery(id+"F1.opExtrude","SWEPT_EDGE",EDGE,{"disambiguationData":[OSD([sQuery(id+"F0.wireOp",EDGE,"E4.top"),sQuery(id+"F0.wireOp",EDGE,"E4.right")])]});
            var Q10;
            Q10=makeQuery(id+"F3.opExtrude","SWEPT_EDGE",EDGE,{"disambiguationData":[OSD([sQuery(id+"F2.wireOp",EDGE,"E5.right"),sQuery(id+"F2.wireOp",EDGE,"E6.bottom"),sQuery(id+"F2.wireOp",EDGE,"E6.left")])]});
            var Q11;
            Q11=makeQuery(id+"F1.opExtrude","SWEPT_EDGE",EDGE,{"disambiguationData":[OSD([sQuery(id+"F0.wireOp",EDGE,"E0.right"),sQuery(id+"F0.wireOp",EDGE,"E4.top"),sQuery(id+"F0.wireOp",EDGE,"E4.left")])]});
            var Q12;
            Q12=makeQuery(id+"F3.opExtrude","SWEPT_EDGE",EDGE,{"disambiguationData":[OSD([sQuery(id+"F2.wireOp",EDGE,"E6.top"),sQuery(id+"F2.wireOp",EDGE,"E6.right")])]});
            var Q13;
            Q13=makeQuery(id+"F1.opExtrude","SWEPT_EDGE",EDGE,{"disambiguationData":[OSD([sQuery(id+"F0.wireOp",EDGE,"E4.bottom"),sQuery(id+"F0.wireOp",EDGE,"E4.right")])]});
            var Q14;
            Q14=makeQuery(id+"F3.opExtrude","SWEPT_EDGE",EDGE,{"disambiguationData":[OSD([sQuery(id+"F2.wireOp",EDGE,"E5.right"),sQuery(id+"F2.wireOp",EDGE,"E6.top"),sQuery(id+"F2.wireOp",EDGE,"E6.left")])]});
            var Q15;
            Q15=makeQuery(id+"F1.opExtrude","SWEPT_EDGE",EDGE,{"disambiguationData":[OSD([sQuery(id+"F0.wireOp",EDGE,"E0.right"),sQuery(id+"F0.wireOp",EDGE,"E4.bottom"),sQuery(id+"F0.wireOp",EDGE,"E4.left")])]});
            fillet(context, id + "F4", {"entities" : qUnion([Q0, Q1, Q2, Q3, Q4, Q5, Q6, Q7, Q8, Q9, Q10, Q11, Q12, Q13, Q14, Q15]), "radius" : 3 * mm, "tangentPropagation" : true, "allowEdgeOverflow" : false});
        }
        {
            var Q0;
            Q0=makeQuery(id+"F1.opExtrude","CAP_FACE",FACE,{"disambiguationData":[OSD([sQuery(id+"F0.wireOp",EDGE,"E0.bottom"),sQuery(id+"F0.wireOp",EDGE,"E0.top"),sQuery(id+"F0.wireOp",EDGE,"E0.left"),sQuery(id+"F0.wireOp",EDGE,"E0.right"),sQuery(id+"F0.wireOp",EDGE,"E1.sketch_text.stroke-0"),sQuery(id+"F0.wireOp",EDGE,"E1.sketch_text.stroke-1"),sQuery(id+"F0.wireOp",EDGE,"E1.sketch_text.stroke-2"),sQuery(id+"F0.wireOp",EDGE,"E1.sketch_text.stroke-3"),sQuery(id+"F0.wireOp",EDGE,"E1.sketch_text.stroke-4"),sQuery(id+"F0.wireOp",EDGE,"E1.sketch_text.stroke-5"),sQuery(id+"F0.wireOp",EDGE,"E1.sketch_text.stroke-6"),sQuery(id+"F0.wireOp",EDGE,"E1.sketch_text.stroke-7"),sQuery(id+"F0.wireOp",EDGE,"E1.sketch_text.stroke-8"),sQuery(id+"F0.wireOp",EDGE,"E1.sketch_text.stroke-9"),sQuery(id+"F0.wireOp",EDGE,"E1.sketch_text.stroke-10"),sQuery(id+"F0.wireOp",EDGE,"E1.sketch_text.stroke-11"),sQuery(id+"F0.wireOp",EDGE,"E1.sketch_text.stroke-12"),sQuery(id+"F0.wireOp",EDGE,"E1.sketch_text.stroke-13"),sQuery(id+"F0.wireOp",EDGE,"E1.sketch_text.stroke-14"),sQuery(id+"F0.wireOp",EDGE,"E1.sketch_text.stroke-15"),sQuery(id+"F0.wireOp",EDGE,"E1.sketch_text.stroke-16"),sQuery(id+"F0.wireOp",EDGE,"E1.sketch_text.stroke-17"),sQuery(id+"F0.wireOp",EDGE,"E1.sketch_text.stroke-18"),sQuery(id+"F0.wireOp",EDGE,"E1.sketch_text.stroke-19"),sQuery(id+"F0.wireOp",EDGE,"E1.sketch_text.stroke-20"),sQuery(id+"F0.wireOp",EDGE,"E1.sketch_text.stroke-21"),sQuery(id+"F0.wireOp",EDGE,"E1.sketch_text.stroke-22"),sQuery(id+"F0.wireOp",EDGE,"E1.sketch_text.stroke-23"),sQuery(id+"F0.wireOp",EDGE,"E1.sketch_text.stroke-24"),sQuery(id+"F0.wireOp",EDGE,"E1.sketch_text.stroke-25"),sQuery(id+"F0.wireOp",EDGE,"E1.sketch_text.stroke-26"),sQuery(id+"F0.wireOp",EDGE,"E1.sketch_text.stroke-27"),sQuery(id+"F0.wireOp",EDGE,"E1.sketch_text.stroke-28"),sQuery(id+"F0.wireOp",EDGE,"E1.sketch_text.stroke-29"),sQuery(id+"F0.wireOp",EDGE,"E1.sketch_text.stroke-30"),sQuery(id+"F0.wireOp",EDGE,"E1.sketch_text.stroke-31"),sQuery(id+"F0.wireOp",EDGE,"E1.sketch_text.stroke-32"),sQuery(id+"F0.wireOp",EDGE,"E1.sketch_text.stroke-33"),sQuery(id+"F0.wireOp",EDGE,"E1.sketch_text.stroke-34"),sQuery(id+"F0.wireOp",EDGE,"E1.sketch_text.stroke-35"),sQuery(id+"F0.wireOp",EDGE,"E1.sketch_text.stroke-36"),sQuery(id+"F0.wireOp",EDGE,"E1.sketch_text.stroke-37"),sQuery(id+"F0.wireOp",EDGE,"E1.sketch_text.stroke-38"),sQuery(id+"F0.wireOp",EDGE,"E1.sketch_text.stroke-39"),sQuery(id+"F0.wireOp",EDGE,"E1.sketch_text.stroke-40"),sQuery(id+"F0.wireOp",EDGE,"E1.sketch_text.stroke-41"),sQuery(id+"F0.wireOp",EDGE,"E1.sketch_text.stroke-42"),sQuery(id+"F0.wireOp",EDGE,"E1.sketch_text.stroke-43"),sQuery(id+"F0.wireOp",EDGE,"E1.sketch_text.stroke-44"),sQuery(id+"F0.wireOp",EDGE,"E1.sketch_text.stroke-45"),sQuery(id+"F0.wireOp",EDGE,"E1.sketch_text.stroke-46"),sQuery(id+"F0.wireOp",EDGE,"E1.sketch_text.stroke-47"),sQuery(id+"F0.wireOp",EDGE,"E1.sketch_text.stroke-48"),sQuery(id+"F0.wireOp",EDGE,"E1.sketch_text.stroke-49"),sQuery(id+"F0.wireOp",EDGE,"E1.sketch_text.stroke-55"),sQuery(id+"F0.wireOp",EDGE,"E1.sketch_text.stroke-56"),sQuery(id+"F0.wireOp",EDGE,"E1.sketch_text.stroke-57"),sQuery(id+"F0.wireOp",EDGE,"E1.sketch_text.stroke-58"),sQuery(id+"F0.wireOp",EDGE,"E1.sketch_text.stroke-59"),sQuery(id+"F0.wireOp",EDGE,"E1.sketch_text.stroke-60"),sQuery(id+"F0.wireOp",EDGE,"E1.sketch_text.stroke-61"),sQuery(id+"F0.wireOp",EDGE,"E1.sketch_text.stroke-62"),sQuery(id+"F0.wireOp",EDGE,"E1.sketch_text.stroke-63"),sQuery(id+"F0.wireOp",EDGE,"E1.sketch_text.stroke-64"),sQuery(id+"F0.wireOp",EDGE,"E1.sketch_text.stroke-65"),sQuery(id+"F0.wireOp",EDGE,"E1.sketch_text.stroke-66"),sQuery(id+"F0.wireOp",EDGE,"E1.sketch_text.stroke-67"),sQuery(id+"F0.wireOp",EDGE,"E1.sketch_text.stroke-68"),sQuery(id+"F0.wireOp",EDGE,"E1.sketch_text.stroke-69"),sQuery(id+"F0.wireOp",EDGE,"E1.sketch_text.stroke-70"),sQuery(id+"F0.wireOp",EDGE,"E1.sketch_text.stroke-71"),sQuery(id+"F0.wireOp",EDGE,"E1.sketch_text.stroke-72"),sQuery(id+"F0.wireOp",EDGE,"E1.sketch_text.stroke-73"),sQuery(id+"F0.wireOp",EDGE,"E1.sketch_text.stroke-74"),sQuery(id+"F0.wireOp",EDGE,"E1.sketch_text.stroke-75"),sQuery(id+"F0.wireOp",EDGE,"E1.sketch_text.stroke-76"),sQuery(id+"F0.wireOp",EDGE,"E1.sketch_text.stroke-77"),sQuery(id+"F0.wireOp",EDGE,"E1.sketch_text.stroke-78"),sQuery(id+"F0.wireOp",EDGE,"E1.sketch_text.stroke-79"),sQuery(id+"F0.wireOp",EDGE,"E1.sketch_text.stroke-80"),sQuery(id+"F0.wireOp",EDGE,"E1.sketch_text.stroke-81"),sQuery(id+"F0.wireOp",EDGE,"E1.sketch_text.stroke-82"),sQuery(id+"F0.wireOp",EDGE,"E1.sketch_text.stroke-83"),sQuery(id+"F0.wireOp",EDGE,"E1.sketch_text.stroke-84"),sQuery(id+"F0.wireOp",EDGE,"E1.sketch_text.stroke-85"),sQuery(id+"F0.wireOp",EDGE,"E1.sketch_text.stroke-86"),sQuery(id+"F0.wireOp",EDGE,"E1.sketch_text.stroke-87"),sQuery(id+"F0.wireOp",EDGE,"E1.sketch_text.stroke-88"),sQuery(id+"F0.wireOp",EDGE,"E1.sketch_text.stroke-94"),sQuery(id+"F0.wireOp",EDGE,"E1.sketch_text.stroke-95"),sQuery(id+"F0.wireOp",EDGE,"E1.sketch_text.stroke-96"),sQuery(id+"F0.wireOp",EDGE,"E1.sketch_text.stroke-97"),sQuery(id+"F0.wireOp",EDGE,"E1.sketch_text.stroke-98"),sQuery(id+"F0.wireOp",EDGE,"E1.sketch_text.stroke-99"),sQuery(id+"F0.wireOp",EDGE,"E1.sketch_text.stroke-100"),sQuery(id+"F0.wireOp",EDGE,"E1.sketch_text.stroke-101"),sQuery(id+"F0.wireOp",EDGE,"E1.sketch_text.stroke-102"),sQuery(id+"F0.wireOp",EDGE,"E1.sketch_text.stroke-103"),sQuery(id+"F0.wireOp",EDGE,"E1.sketch_text.stroke-104"),sQuery(id+"F0.wireOp",EDGE,"E1.sketch_text.stroke-105"),sQuery(id+"F0.wireOp",EDGE,"E1.sketch_text.stroke-106"),sQuery(id+"F0.wireOp",EDGE,"E1.sketch_text.stroke-107"),sQuery(id+"F0.wireOp",EDGE,"E1.sketch_text.stroke-108"),sQuery(id+"F0.wireOp",EDGE,"E1.sketch_text.stroke-109"),sQuery(id+"F0.wireOp",EDGE,"E1.sketch_text.stroke-110"),sQuery(id+"F0.wireOp",EDGE,"E1.sketch_text.stroke-111"),sQuery(id+"F0.wireOp",EDGE,"E1.sketch_text.stroke-112"),sQuery(id+"F0.wireOp",EDGE,"E1.sketch_text.stroke-113"),sQuery(id+"F0.wireOp",EDGE,"E1.sketch_text.stroke-114"),sQuery(id+"F0.wireOp",EDGE,"E1.sketch_text.stroke-115"),sQuery(id+"F0.wireOp",EDGE,"E1.sketch_text.stroke-116"),sQuery(id+"F0.wireOp",EDGE,"E1.sketch_text.stroke-117"),sQuery(id+"F0.wireOp",EDGE,"E1.sketch_text.stroke-118"),sQuery(id+"F0.wireOp",EDGE,"E1.sketch_text.stroke-119"),sQuery(id+"F0.wireOp",EDGE,"E1.sketch_text.stroke-120"),sQuery(id+"F0.wireOp",EDGE,"E1.sketch_text.stroke-121"),sQuery(id+"F0.wireOp",EDGE,"E1.sketch_text.stroke-122"),sQuery(id+"F0.wireOp",EDGE,"E1.sketch_text.stroke-123"),sQuery(id+"F0.wireOp",EDGE,"E1.sketch_text.stroke-124"),sQuery(id+"F0.wireOp",EDGE,"E1.sketch_text.stroke-125"),sQuery(id+"F0.wireOp",EDGE,"E1.sketch_text.stroke-126"),sQuery(id+"F0.wireOp",EDGE,"E1.sketch_text.stroke-127"),sQuery(id+"F0.wireOp",EDGE,"E1.sketch_text.stroke-128"),sQuery(id+"F0.wireOp",EDGE,"E1.sketch_text.stroke-129"),sQuery(id+"F0.wireOp",EDGE,"E1.sketch_text.stroke-130"),sQuery(id+"F0.wireOp",EDGE,"E1.sketch_text.stroke-131"),sQuery(id+"F0.wireOp",EDGE,"E1.sketch_text.stroke-139"),sQuery(id+"F0.wireOp",EDGE,"E1.sketch_text.stroke-140"),sQuery(id+"F0.wireOp",EDGE,"E1.sketch_text.stroke-141"),sQuery(id+"F0.wireOp",EDGE,"E1.sketch_text.stroke-142"),sQuery(id+"F0.wireOp",EDGE,"E1.sketch_text.stroke-143"),sQuery(id+"F0.wireOp",EDGE,"E1.sketch_text.stroke-144"),sQuery(id+"F0.wireOp",EDGE,"E1.sketch_text.stroke-145"),sQuery(id+"F0.wireOp",EDGE,"E1.sketch_text.stroke-146"),sQuery(id+"F0.wireOp",EDGE,"E1.sketch_text.stroke-147"),sQuery(id+"F0.wireOp",EDGE,"E1.sketch_text.stroke-148"),sQuery(id+"F0.wireOp",EDGE,"E1.sketch_text.stroke-149"),sQuery(id+"F0.wireOp",EDGE,"E1.sketch_text.stroke-150"),sQuery(id+"F0.wireOp",EDGE,"E1.sketch_text.stroke-151"),sQuery(id+"F0.wireOp",EDGE,"E1.sketch_text.stroke-152"),sQuery(id+"F0.wireOp",EDGE,"E1.sketch_text.stroke-153"),sQuery(id+"F0.wireOp",EDGE,"E1.sketch_text.stroke-154"),sQuery(id+"F0.wireOp",EDGE,"E1.sketch_text.stroke-155"),sQuery(id+"F0.wireOp",EDGE,"E1.sketch_text.stroke-156"),sQuery(id+"F0.wireOp",EDGE,"E1.sketch_text.stroke-157"),sQuery(id+"F0.wireOp",EDGE,"E1.sketch_text.stroke-166"),sQuery(id+"F0.wireOp",EDGE,"E1.sketch_text.stroke-167"),sQuery(id+"F0.wireOp",EDGE,"E1.sketch_text.stroke-168"),sQuery(id+"F0.wireOp",EDGE,"E1.sketch_text.stroke-169"),sQuery(id+"F0.wireOp",EDGE,"E1.sketch_text.stroke-170"),sQuery(id+"F0.wireOp",EDGE,"E1.sketch_text.stroke-171"),sQuery(id+"F0.wireOp",EDGE,"E1.sketch_text.stroke-172"),sQuery(id+"F0.wireOp",EDGE,"E1.sketch_text.stroke-173"),sQuery(id+"F0.wireOp",EDGE,"E1.sketch_text.stroke-174"),sQuery(id+"F0.wireOp",EDGE,"E1.sketch_text.stroke-175"),sQuery(id+"F0.wireOp",EDGE,"E1.sketch_text.stroke-176"),sQuery(id+"F0.wireOp",EDGE,"E1.sketch_text.stroke-177"),sQuery(id+"F0.wireOp",EDGE,"E1.sketch_text.stroke-178"),sQuery(id+"F0.wireOp",EDGE,"E1.sketch_text.stroke-179"),sQuery(id+"F0.wireOp",EDGE,"E1.sketch_text.stroke-180"),sQuery(id+"F0.wireOp",EDGE,"E1.sketch_text.stroke-181"),sQuery(id+"F0.wireOp",EDGE,"E1.sketch_text.stroke-191"),sQuery(id+"F0.wireOp",EDGE,"E1.sketch_text.stroke-192"),sQuery(id+"F0.wireOp",EDGE,"E1.sketch_text.stroke-193"),sQuery(id+"F0.wireOp",EDGE,"E1.sketch_text.stroke-194"),sQuery(id+"F0.wireOp",EDGE,"E1.sketch_text.stroke-195"),sQuery(id+"F0.wireOp",EDGE,"E1.sketch_text.stroke-196"),sQuery(id+"F0.wireOp",EDGE,"E1.sketch_text.stroke-197"),sQuery(id+"F0.wireOp",EDGE,"E1.sketch_text.stroke-198"),sQuery(id+"F0.wireOp",EDGE,"E1.sketch_text.stroke-199"),sQuery(id+"F0.wireOp",EDGE,"E1.sketch_text.stroke-200"),sQuery(id+"F0.wireOp",EDGE,"E1.sketch_text.stroke-201"),sQuery(id+"F0.wireOp",EDGE,"E1.sketch_text.stroke-202"),sQuery(id+"F0.wireOp",EDGE,"E1.sketch_text.stroke-203"),sQuery(id+"F0.wireOp",EDGE,"E1.sketch_text.stroke-204"),sQuery(id+"F0.wireOp",EDGE,"E1.sketch_text.stroke-205"),sQuery(id+"F0.wireOp",EDGE,"E1.sketch_text.stroke-206"),sQuery(id+"F0.wireOp",EDGE,"E1.sketch_text.stroke-207"),sQuery(id+"F0.wireOp",EDGE,"E1.sketch_text.stroke-208"),sQuery(id+"F0.wireOp",EDGE,"E1.sketch_text.stroke-209"),sQuery(id+"F0.wireOp",EDGE,"E3.sketch_text.stroke-0"),sQuery(id+"F0.wireOp",EDGE,"E3.sketch_text.stroke-1"),sQuery(id+"F0.wireOp",EDGE,"E3.sketch_text.stroke-2"),sQuery(id+"F0.wireOp",EDGE,"E3.sketch_text.stroke-3"),sQuery(id+"F0.wireOp",EDGE,"E3.sketch_text.stroke-4"),sQuery(id+"F0.wireOp",EDGE,"E3.sketch_text.stroke-5"),sQuery(id+"F0.wireOp",EDGE,"E3.sketch_text.stroke-6"),sQuery(id+"F0.wireOp",EDGE,"E3.sketch_text.stroke-7"),sQuery(id+"F0.wireOp",EDGE,"E3.sketch_text.stroke-8"),sQuery(id+"F0.wireOp",EDGE,"E3.sketch_text.stroke-9"),sQuery(id+"F0.wireOp",EDGE,"E3.sketch_text.stroke-10"),sQuery(id+"F0.wireOp",EDGE,"E3.sketch_text.stroke-11"),sQuery(id+"F0.wireOp",EDGE,"E3.sketch_text.stroke-12"),sQuery(id+"F0.wireOp",EDGE,"E3.sketch_text.stroke-13"),sQuery(id+"F0.wireOp",EDGE,"E3.sketch_text.stroke-14"),sQuery(id+"F0.wireOp",EDGE,"E3.sketch_text.stroke-24"),sQuery(id+"F0.wireOp",EDGE,"E3.sketch_text.stroke-25"),sQuery(id+"F0.wireOp",EDGE,"E3.sketch_text.stroke-26"),sQuery(id+"F0.wireOp",EDGE,"E3.sketch_text.stroke-27"),sQuery(id+"F0.wireOp",EDGE,"E3.sketch_text.stroke-28"),sQuery(id+"F0.wireOp",EDGE,"E3.sketch_text.stroke-29"),sQuery(id+"F0.wireOp",EDGE,"E3.sketch_text.stroke-30"),sQuery(id+"F0.wireOp",EDGE,"E3.sketch_text.stroke-31"),sQuery(id+"F0.wireOp",EDGE,"E3.sketch_text.stroke-32"),sQuery(id+"F0.wireOp",EDGE,"E3.sketch_text.stroke-33"),sQuery(id+"F0.wireOp",EDGE,"E3.sketch_text.stroke-34"),sQuery(id+"F0.wireOp",EDGE,"E3.sketch_text.stroke-35"),sQuery(id+"F0.wireOp",EDGE,"E3.sketch_text.stroke-36"),sQuery(id+"F0.wireOp",EDGE,"E3.sketch_text.stroke-37"),sQuery(id+"F0.wireOp",EDGE,"E3.sketch_text.stroke-43"),sQuery(id+"F0.wireOp",EDGE,"E3.sketch_text.stroke-44"),sQuery(id+"F0.wireOp",EDGE,"E3.sketch_text.stroke-45"),sQuery(id+"F0.wireOp",EDGE,"E3.sketch_text.stroke-46"),sQuery(id+"F0.wireOp",EDGE,"E3.sketch_text.stroke-47"),sQuery(id+"F0.wireOp",EDGE,"E3.sketch_text.stroke-48"),sQuery(id+"F0.wireOp",EDGE,"E3.sketch_text.stroke-49"),sQuery(id+"F0.wireOp",EDGE,"E3.sketch_text.stroke-50"),sQuery(id+"F0.wireOp",EDGE,"E3.sketch_text.stroke-51"),sQuery(id+"F0.wireOp",EDGE,"E3.sketch_text.stroke-52"),sQuery(id+"F0.wireOp",EDGE,"E3.sketch_text.stroke-53"),sQuery(id+"F0.wireOp",EDGE,"E3.sketch_text.stroke-54"),sQuery(id+"F0.wireOp",EDGE,"E3.sketch_text.stroke-55"),sQuery(id+"F0.wireOp",EDGE,"E3.sketch_text.stroke-56"),sQuery(id+"F0.wireOp",EDGE,"E3.sketch_text.stroke-57"),sQuery(id+"F0.wireOp",EDGE,"E3.sketch_text.stroke-58"),sQuery(id+"F0.wireOp",EDGE,"E3.sketch_text.stroke-59"),sQuery(id+"F0.wireOp",EDGE,"E3.sketch_text.stroke-60"),sQuery(id+"F0.wireOp",EDGE,"E3.sketch_text.stroke-61"),sQuery(id+"F0.wireOp",EDGE,"E3.sketch_text.stroke-62"),sQuery(id+"F0.wireOp",EDGE,"E3.sketch_text.stroke-63"),sQuery(id+"F0.wireOp",EDGE,"E3.sketch_text.stroke-64"),sQuery(id+"F0.wireOp",EDGE,"E3.sketch_text.stroke-65"),sQuery(id+"F0.wireOp",EDGE,"E3.sketch_text.stroke-74"),sQuery(id+"F0.wireOp",EDGE,"E3.sketch_text.stroke-75"),sQuery(id+"F0.wireOp",EDGE,"E3.sketch_text.stroke-76"),sQuery(id+"F0.wireOp",EDGE,"E3.sketch_text.stroke-77"),sQuery(id+"F0.wireOp",EDGE,"E3.sketch_text.stroke-78"),sQuery(id+"F0.wireOp",EDGE,"E3.sketch_text.stroke-79"),sQuery(id+"F0.wireOp",EDGE,"E3.sketch_text.stroke-80"),sQuery(id+"F0.wireOp",EDGE,"E3.sketch_text.stroke-81"),sQuery(id+"F0.wireOp",EDGE,"E3.sketch_text.stroke-82"),sQuery(id+"F0.wireOp",EDGE,"E3.sketch_text.stroke-83"),sQuery(id+"F0.wireOp",EDGE,"E3.sketch_text.stroke-84"),sQuery(id+"F0.wireOp",EDGE,"E3.sketch_text.stroke-85"),sQuery(id+"F0.wireOp",EDGE,"E3.sketch_text.stroke-86"),sQuery(id+"F0.wireOp",EDGE,"E3.sketch_text.stroke-87"),sQuery(id+"F0.wireOp",EDGE,"E3.sketch_text.stroke-88"),sQuery(id+"F0.wireOp",EDGE,"E3.sketch_text.stroke-89"),sQuery(id+"F0.wireOp",EDGE,"E3.sketch_text.stroke-90"),sQuery(id+"F0.wireOp",EDGE,"E3.sketch_text.stroke-91"),sQuery(id+"F0.wireOp",EDGE,"E3.sketch_text.stroke-92"),sQuery(id+"F0.wireOp",EDGE,"E3.sketch_text.stroke-93"),sQuery(id+"F0.wireOp",EDGE,"E3.sketch_text.stroke-94"),sQuery(id+"F0.wireOp",EDGE,"E3.sketch_text.stroke-95"),sQuery(id+"F0.wireOp",EDGE,"E3.sketch_text.stroke-96"),sQuery(id+"F0.wireOp",EDGE,"E3.sketch_text.stroke-97"),sQuery(id+"F0.wireOp",EDGE,"E3.sketch_text.stroke-98"),sQuery(id+"F0.wireOp",EDGE,"E3.sketch_text.stroke-99"),sQuery(id+"F0.wireOp",EDGE,"E3.sketch_text.stroke-100"),sQuery(id+"F0.wireOp",EDGE,"E3.sketch_text.stroke-101"),sQuery(id+"F0.wireOp",EDGE,"E3.sketch_text.stroke-102"),sQuery(id+"F0.wireOp",EDGE,"E3.sketch_text.stroke-103"),sQuery(id+"F0.wireOp",EDGE,"E3.sketch_text.stroke-104"),sQuery(id+"F0.wireOp",EDGE,"E3.sketch_text.stroke-105"),sQuery(id+"F0.wireOp",EDGE,"E3.sketch_text.stroke-106"),sQuery(id+"F0.wireOp",EDGE,"E3.sketch_text.stroke-107"),sQuery(id+"F0.wireOp",EDGE,"E3.sketch_text.stroke-108"),sQuery(id+"F0.wireOp",EDGE,"E3.sketch_text.stroke-109"),sQuery(id+"F0.wireOp",EDGE,"E3.sketch_text.stroke-110"),sQuery(id+"F0.wireOp",EDGE,"E3.sketch_text.stroke-111"),sQuery(id+"F0.wireOp",EDGE,"E3.sketch_text.stroke-112"),sQuery(id+"F0.wireOp",EDGE,"E3.sketch_text.stroke-121"),sQuery(id+"F0.wireOp",EDGE,"E3.sketch_text.stroke-122"),sQuery(id+"F0.wireOp",EDGE,"E3.sketch_text.stroke-123"),sQuery(id+"F0.wireOp",EDGE,"E3.sketch_text.stroke-124"),sQuery(id+"F0.wireOp",EDGE,"E3.sketch_text.stroke-125"),sQuery(id+"F0.wireOp",EDGE,"E3.sketch_text.stroke-126"),sQuery(id+"F0.wireOp",EDGE,"E3.sketch_text.stroke-127"),sQuery(id+"F0.wireOp",EDGE,"E3.sketch_text.stroke-128"),sQuery(id+"F0.wireOp",EDGE,"E3.sketch_text.stroke-129"),sQuery(id+"F0.wireOp",EDGE,"E3.sketch_text.stroke-130"),sQuery(id+"F0.wireOp",EDGE,"E3.sketch_text.stroke-131"),sQuery(id+"F0.wireOp",EDGE,"E3.sketch_text.stroke-132"),sQuery(id+"F0.wireOp",EDGE,"E3.sketch_text.stroke-133"),sQuery(id+"F0.wireOp",EDGE,"E3.sketch_text.stroke-134"),sQuery(id+"F0.wireOp",EDGE,"E3.sketch_text.stroke-135"),sQuery(id+"F0.wireOp",EDGE,"E3.sketch_text.stroke-136"),sQuery(id+"F0.wireOp",EDGE,"E3.sketch_text.stroke-137"),sQuery(id+"F0.wireOp",EDGE,"E3.sketch_text.stroke-138"),sQuery(id+"F0.wireOp",EDGE,"E3.sketch_text.stroke-139"),sQuery(id+"F0.wireOp",EDGE,"E3.sketch_text.stroke-140"),sQuery(id+"F0.wireOp",EDGE,"E3.sketch_text.stroke-141"),sQuery(id+"F0.wireOp",EDGE,"E3.sketch_text.stroke-142"),sQuery(id+"F0.wireOp",EDGE,"E3.sketch_text.stroke-143"),sQuery(id+"F0.wireOp",EDGE,"E3.sketch_text.stroke-152"),sQuery(id+"F0.wireOp",EDGE,"E3.sketch_text.stroke-153"),sQuery(id+"F0.wireOp",EDGE,"E3.sketch_text.stroke-154"),sQuery(id+"F0.wireOp",EDGE,"E3.sketch_text.stroke-155"),sQuery(id+"F0.wireOp",EDGE,"E3.sketch_text.stroke-156"),sQuery(id+"F0.wireOp",EDGE,"E3.sketch_text.stroke-157"),sQuery(id+"F0.wireOp",EDGE,"E3.sketch_text.stroke-158"),sQuery(id+"F0.wireOp",EDGE,"E3.sketch_text.stroke-159"),sQuery(id+"F0.wireOp",EDGE,"E3.sketch_text.stroke-160"),sQuery(id+"F0.wireOp",EDGE,"E3.sketch_text.stroke-161"),sQuery(id+"F0.wireOp",EDGE,"E3.sketch_text.stroke-162"),sQuery(id+"F0.wireOp",EDGE,"E3.sketch_text.stroke-163"),sQuery(id+"F0.wireOp",EDGE,"E3.sketch_text.stroke-164"),sQuery(id+"F0.wireOp",EDGE,"E3.sketch_text.stroke-165"),sQuery(id+"F0.wireOp",EDGE,"E3.sketch_text.stroke-166"),sQuery(id+"F0.wireOp",EDGE,"E3.sketch_text.stroke-167"),sQuery(id+"F0.wireOp",EDGE,"E3.sketch_text.stroke-168"),sQuery(id+"F0.wireOp",EDGE,"E3.sketch_text.stroke-169"),sQuery(id+"F0.wireOp",EDGE,"E3.sketch_text.stroke-170"),sQuery(id+"F0.wireOp",EDGE,"E3.sketch_text.stroke-171"),sQuery(id+"F0.wireOp",EDGE,"E3.sketch_text.stroke-172"),sQuery(id+"F0.wireOp",EDGE,"E3.sketch_text.stroke-173"),sQuery(id+"F0.wireOp",EDGE,"E3.sketch_text.stroke-174"),sQuery(id+"F0.wireOp",EDGE,"E3.sketch_text.stroke-175"),sQuery(id+"F0.wireOp",EDGE,"E3.sketch_text.stroke-176"),sQuery(id+"F0.wireOp",EDGE,"E3.sketch_text.stroke-177"),sQuery(id+"F0.wireOp",EDGE,"E3.sketch_text.stroke-178"),sQuery(id+"F0.wireOp",EDGE,"E3.sketch_text.stroke-179"),sQuery(id+"F0.wireOp",EDGE,"E3.sketch_text.stroke-180"),sQuery(id+"F0.wireOp",EDGE,"E3.sketch_text.stroke-181"),sQuery(id+"F0.wireOp",EDGE,"E3.sketch_text.stroke-182"),sQuery(id+"F0.wireOp",EDGE,"E3.sketch_text.stroke-183"),sQuery(id+"F0.wireOp",EDGE,"E3.sketch_text.stroke-184"),sQuery(id+"F0.wireOp",EDGE,"E3.sketch_text.stroke-185"),sQuery(id+"F0.wireOp",EDGE,"E3.sketch_text.stroke-186"),sQuery(id+"F0.wireOp",EDGE,"E3.sketch_text.stroke-187"),sQuery(id+"F0.wireOp",EDGE,"E3.sketch_text.stroke-188"),sQuery(id+"F0.wireOp",EDGE,"E3.sketch_text.stroke-189"),sQuery(id+"F0.wireOp",EDGE,"E3.sketch_text.stroke-195"),sQuery(id+"F0.wireOp",EDGE,"E3.sketch_text.stroke-196"),sQuery(id+"F0.wireOp",EDGE,"E3.sketch_text.stroke-197"),sQuery(id+"F0.wireOp",EDGE,"E3.sketch_text.stroke-198"),sQuery(id+"F0.wireOp",EDGE,"E3.sketch_text.stroke-199"),sQuery(id+"F0.wireOp",EDGE,"E3.sketch_text.stroke-200"),sQuery(id+"F0.wireOp",EDGE,"E3.sketch_text.stroke-201"),sQuery(id+"F0.wireOp",EDGE,"E3.sketch_text.stroke-202"),sQuery(id+"F0.wireOp",EDGE,"E3.sketch_text.stroke-203"),sQuery(id+"F0.wireOp",EDGE,"E3.sketch_text.stroke-204"),sQuery(id+"F0.wireOp",EDGE,"E3.sketch_text.stroke-205"),sQuery(id+"F0.wireOp",EDGE,"E3.sketch_text.stroke-206"),sQuery(id+"F0.wireOp",EDGE,"E3.sketch_text.stroke-207"),sQuery(id+"F0.wireOp",EDGE,"E3.sketch_text.stroke-208"),sQuery(id+"F0.wireOp",EDGE,"E3.sketch_text.stroke-209"),sQuery(id+"F0.wireOp",EDGE,"E3.sketch_text.stroke-210"),sQuery(id+"F0.wireOp",EDGE,"E3.sketch_text.stroke-211"),sQuery(id+"F0.wireOp",EDGE,"E3.sketch_text.stroke-212"),sQuery(id+"F0.wireOp",EDGE,"E3.sketch_text.stroke-213"),sQuery(id+"F0.wireOp",EDGE,"E3.sketch_text.stroke-214"),sQuery(id+"F0.wireOp",EDGE,"E3.sketch_text.stroke-215"),sQuery(id+"F0.wireOp",EDGE,"E3.sketch_text.stroke-216"),sQuery(id+"F0.wireOp",EDGE,"E3.sketch_text.stroke-217"),sQuery(id+"F0.wireOp",EDGE,"E3.sketch_text.stroke-218"),sQuery(id+"F0.wireOp",EDGE,"E3.sketch_text.stroke-219"),sQuery(id+"F0.wireOp",EDGE,"E3.sketch_text.stroke-220"),sQuery(id+"F0.wireOp",EDGE,"E3.sketch_text.stroke-221"),sQuery(id+"F0.wireOp",EDGE,"E3.sketch_text.stroke-222"),sQuery(id+"F0.wireOp",EDGE,"E3.sketch_text.stroke-223"),sQuery(id+"F0.wireOp",EDGE,"E3.sketch_text.stroke-224"),sQuery(id+"F0.wireOp",EDGE,"E3.sketch_text.stroke-225"),sQuery(id+"F0.wireOp",EDGE,"E3.sketch_text.stroke-226"),sQuery(id+"F0.wireOp",EDGE,"E3.sketch_text.stroke-227"),sQuery(id+"F0.wireOp",EDGE,"E3.sketch_text.stroke-228"),sQuery(id+"F0.wireOp",EDGE,"E3.sketch_text.stroke-229"),sQuery(id+"F0.wireOp",EDGE,"E3.sketch_text.stroke-230"),sQuery(id+"F0.wireOp",EDGE,"E3.sketch_text.stroke-231"),sQuery(id+"F0.wireOp",EDGE,"E3.sketch_text.stroke-232"),sQuery(id+"F0.wireOp",EDGE,"E3.sketch_text.stroke-233"),sQuery(id+"F0.wireOp",EDGE,"E3.sketch_text.stroke-234"),sQuery(id+"F0.wireOp",EDGE,"E3.sketch_text.stroke-235"),sQuery(id+"F0.wireOp",EDGE,"E3.sketch_text.stroke-236"),sQuery(id+"F0.wireOp",EDGE,"E3.sketch_text.stroke-237"),sQuery(id+"F0.wireOp",EDGE,"E3.sketch_text.stroke-238"),sQuery(id+"F0.wireOp",EDGE,"E3.sketch_text.stroke-239"),sQuery(id+"F0.wireOp",EDGE,"E3.sketch_text.stroke-240"),sQuery(id+"F0.wireOp",EDGE,"E4.bottom"),sQuery(id+"F0.wireOp",EDGE,"E4.top"),sQuery(id+"F0.wireOp",EDGE,"E4.right")])],"isStart":false});
            var sketch = newSketch(context, id + "F5", { "sketchPlane" : qUnion([Q0])});
            skLineSegment(sketch, "E7", {"start": v(-34.33, 4.6) * mm, "end": v(-34.33, -4.6) * mm});
            skPoint(sketch, "E8", {"position": v(-34.33, 0) * mm});
            skCircle(sketch, "E9", {"center": v(-34.33, 0) * mm, "radius": 1.57 * mm});
            skSolve(sketch);
        }
        {
            var Q0;
            Q0 = qSketchRegion(id + "F5", true);
            extrude(context, id + "F6", {"entities" : qUnion([Q0]), "operationType" : NewBodyOperationType.REMOVE, "endBound" : BoundingType.THROUGH_ALL, "oppositeDirection" : true, "depth" : 25 * mm});
        }
        {
            var Q0;
            Q0=makeQuery(id+"F1.opExtrude","CAP_FACE",FACE,{"disambiguationData":[OSD([sQuery(id+"F0.wireOp",EDGE,"E0.bottom"),sQuery(id+"F0.wireOp",EDGE,"E0.top"),sQuery(id+"F0.wireOp",EDGE,"E0.left"),sQuery(id+"F0.wireOp",EDGE,"E0.right"),sQuery(id+"F0.wireOp",EDGE,"E1.sketch_text.stroke-0"),sQuery(id+"F0.wireOp",EDGE,"E1.sketch_text.stroke-1"),sQuery(id+"F0.wireOp",EDGE,"E1.sketch_text.stroke-2"),sQuery(id+"F0.wireOp",EDGE,"E1.sketch_text.stroke-3"),sQuery(id+"F0.wireOp",EDGE,"E1.sketch_text.stroke-4"),sQuery(id+"F0.wireOp",EDGE,"E1.sketch_text.stroke-5"),sQuery(id+"F0.wireOp",EDGE,"E1.sketch_text.stroke-6"),sQuery(id+"F0.wireOp",EDGE,"E1.sketch_text.stroke-7"),sQuery(id+"F0.wireOp",EDGE,"E1.sketch_text.stroke-8"),sQuery(id+"F0.wireOp",EDGE,"E1.sketch_text.stroke-9"),sQuery(id+"F0.wireOp",EDGE,"E1.sketch_text.stroke-10"),sQuery(id+"F0.wireOp",EDGE,"E1.sketch_text.stroke-11"),sQuery(id+"F0.wireOp",EDGE,"E1.sketch_text.stroke-12"),sQuery(id+"F0.wireOp",EDGE,"E1.sketch_text.stroke-13"),sQuery(id+"F0.wireOp",EDGE,"E1.sketch_text.stroke-14"),sQuery(id+"F0.wireOp",EDGE,"E1.sketch_text.stroke-15"),sQuery(id+"F0.wireOp",EDGE,"E1.sketch_text.stroke-16"),sQuery(id+"F0.wireOp",EDGE,"E1.sketch_text.stroke-17"),sQuery(id+"F0.wireOp",EDGE,"E1.sketch_text.stroke-18"),sQuery(id+"F0.wireOp",EDGE,"E1.sketch_text.stroke-19"),sQuery(id+"F0.wireOp",EDGE,"E1.sketch_text.stroke-20"),sQuery(id+"F0.wireOp",EDGE,"E1.sketch_text.stroke-21"),sQuery(id+"F0.wireOp",EDGE,"E1.sketch_text.stroke-22"),sQuery(id+"F0.wireOp",EDGE,"E1.sketch_text.stroke-23"),sQuery(id+"F0.wireOp",EDGE,"E1.sketch_text.stroke-24"),sQuery(id+"F0.wireOp",EDGE,"E1.sketch_text.stroke-25"),sQuery(id+"F0.wireOp",EDGE,"E1.sketch_text.stroke-26"),sQuery(id+"F0.wireOp",EDGE,"E1.sketch_text.stroke-27"),sQuery(id+"F0.wireOp",EDGE,"E1.sketch_text.stroke-28"),sQuery(id+"F0.wireOp",EDGE,"E1.sketch_text.stroke-29"),sQuery(id+"F0.wireOp",EDGE,"E1.sketch_text.stroke-30"),sQuery(id+"F0.wireOp",EDGE,"E1.sketch_text.stroke-31"),sQuery(id+"F0.wireOp",EDGE,"E1.sketch_text.stroke-32"),sQuery(id+"F0.wireOp",EDGE,"E1.sketch_text.stroke-33"),sQuery(id+"F0.wireOp",EDGE,"E1.sketch_text.stroke-34"),sQuery(id+"F0.wireOp",EDGE,"E1.sketch_text.stroke-35"),sQuery(id+"F0.wireOp",EDGE,"E1.sketch_text.stroke-36"),sQuery(id+"F0.wireOp",EDGE,"E1.sketch_text.stroke-37"),sQuery(id+"F0.wireOp",EDGE,"E1.sketch_text.stroke-38"),sQuery(id+"F0.wireOp",EDGE,"E1.sketch_text.stroke-39"),sQuery(id+"F0.wireOp",EDGE,"E1.sketch_text.stroke-40"),sQuery(id+"F0.wireOp",EDGE,"E1.sketch_text.stroke-41"),sQuery(id+"F0.wireOp",EDGE,"E1.sketch_text.stroke-42"),sQuery(id+"F0.wireOp",EDGE,"E1.sketch_text.stroke-43"),sQuery(id+"F0.wireOp",EDGE,"E1.sketch_text.stroke-44"),sQuery(id+"F0.wireOp",EDGE,"E1.sketch_text.stroke-45"),sQuery(id+"F0.wireOp",EDGE,"E1.sketch_text.stroke-46"),sQuery(id+"F0.wireOp",EDGE,"E1.sketch_text.stroke-47"),sQuery(id+"F0.wireOp",EDGE,"E1.sketch_text.stroke-48"),sQuery(id+"F0.wireOp",EDGE,"E1.sketch_text.stroke-49"),sQuery(id+"F0.wireOp",EDGE,"E1.sketch_text.stroke-55"),sQuery(id+"F0.wireOp",EDGE,"E1.sketch_text.stroke-56"),sQuery(id+"F0.wireOp",EDGE,"E1.sketch_text.stroke-57"),sQuery(id+"F0.wireOp",EDGE,"E1.sketch_text.stroke-58"),sQuery(id+"F0.wireOp",EDGE,"E1.sketch_text.stroke-59"),sQuery(id+"F0.wireOp",EDGE,"E1.sketch_text.stroke-60"),sQuery(id+"F0.wireOp",EDGE,"E1.sketch_text.stroke-61"),sQuery(id+"F0.wireOp",EDGE,"E1.sketch_text.stroke-62"),sQuery(id+"F0.wireOp",EDGE,"E1.sketch_text.stroke-63"),sQuery(id+"F0.wireOp",EDGE,"E1.sketch_text.stroke-64"),sQuery(id+"F0.wireOp",EDGE,"E1.sketch_text.stroke-65"),sQuery(id+"F0.wireOp",EDGE,"E1.sketch_text.stroke-66"),sQuery(id+"F0.wireOp",EDGE,"E1.sketch_text.stroke-67"),sQuery(id+"F0.wireOp",EDGE,"E1.sketch_text.stroke-68"),sQuery(id+"F0.wireOp",EDGE,"E1.sketch_text.stroke-69"),sQuery(id+"F0.wireOp",EDGE,"E1.sketch_text.stroke-70"),sQuery(id+"F0.wireOp",EDGE,"E1.sketch_text.stroke-71"),sQuery(id+"F0.wireOp",EDGE,"E1.sketch_text.stroke-72"),sQuery(id+"F0.wireOp",EDGE,"E1.sketch_text.stroke-73"),sQuery(id+"F0.wireOp",EDGE,"E1.sketch_text.stroke-74"),sQuery(id+"F0.wireOp",EDGE,"E1.sketch_text.stroke-75"),sQuery(id+"F0.wireOp",EDGE,"E1.sketch_text.stroke-76"),sQuery(id+"F0.wireOp",EDGE,"E1.sketch_text.stroke-77"),sQuery(id+"F0.wireOp",EDGE,"E1.sketch_text.stroke-78"),sQuery(id+"F0.wireOp",EDGE,"E1.sketch_text.stroke-79"),sQuery(id+"F0.wireOp",EDGE,"E1.sketch_text.stroke-80"),sQuery(id+"F0.wireOp",EDGE,"E1.sketch_text.stroke-81"),sQuery(id+"F0.wireOp",EDGE,"E1.sketch_text.stroke-82"),sQuery(id+"F0.wireOp",EDGE,"E1.sketch_text.stroke-83"),sQuery(id+"F0.wireOp",EDGE,"E1.sketch_text.stroke-84"),sQuery(id+"F0.wireOp",EDGE,"E1.sketch_text.stroke-85"),sQuery(id+"F0.wireOp",EDGE,"E1.sketch_text.stroke-86"),sQuery(id+"F0.wireOp",EDGE,"E1.sketch_text.stroke-87"),sQuery(id+"F0.wireOp",EDGE,"E1.sketch_text.stroke-88"),sQuery(id+"F0.wireOp",EDGE,"E1.sketch_text.stroke-94"),sQuery(id+"F0.wireOp",EDGE,"E1.sketch_text.stroke-95"),sQuery(id+"F0.wireOp",EDGE,"E1.sketch_text.stroke-96"),sQuery(id+"F0.wireOp",EDGE,"E1.sketch_text.stroke-97"),sQuery(id+"F0.wireOp",EDGE,"E1.sketch_text.stroke-98"),sQuery(id+"F0.wireOp",EDGE,"E1.sketch_text.stroke-99"),sQuery(id+"F0.wireOp",EDGE,"E1.sketch_text.stroke-100"),sQuery(id+"F0.wireOp",EDGE,"E1.sketch_text.stroke-101"),sQuery(id+"F0.wireOp",EDGE,"E1.sketch_text.stroke-102"),sQuery(id+"F0.wireOp",EDGE,"E1.sketch_text.stroke-103"),sQuery(id+"F0.wireOp",EDGE,"E1.sketch_text.stroke-104"),sQuery(id+"F0.wireOp",EDGE,"E1.sketch_text.stroke-105"),sQuery(id+"F0.wireOp",EDGE,"E1.sketch_text.stroke-106"),sQuery(id+"F0.wireOp",EDGE,"E1.sketch_text.stroke-107"),sQuery(id+"F0.wireOp",EDGE,"E1.sketch_text.stroke-108"),sQuery(id+"F0.wireOp",EDGE,"E1.sketch_text.stroke-109"),sQuery(id+"F0.wireOp",EDGE,"E1.sketch_text.stroke-110"),sQuery(id+"F0.wireOp",EDGE,"E1.sketch_text.stroke-111"),sQuery(id+"F0.wireOp",EDGE,"E1.sketch_text.stroke-112"),sQuery(id+"F0.wireOp",EDGE,"E1.sketch_text.stroke-113"),sQuery(id+"F0.wireOp",EDGE,"E1.sketch_text.stroke-114"),sQuery(id+"F0.wireOp",EDGE,"E1.sketch_text.stroke-115"),sQuery(id+"F0.wireOp",EDGE,"E1.sketch_text.stroke-116"),sQuery(id+"F0.wireOp",EDGE,"E1.sketch_text.stroke-117"),sQuery(id+"F0.wireOp",EDGE,"E1.sketch_text.stroke-118"),sQuery(id+"F0.wireOp",EDGE,"E1.sketch_text.stroke-119"),sQuery(id+"F0.wireOp",EDGE,"E1.sketch_text.stroke-120"),sQuery(id+"F0.wireOp",EDGE,"E1.sketch_text.stroke-121"),sQuery(id+"F0.wireOp",EDGE,"E1.sketch_text.stroke-122"),sQuery(id+"F0.wireOp",EDGE,"E1.sketch_text.stroke-123"),sQuery(id+"F0.wireOp",EDGE,"E1.sketch_text.stroke-124"),sQuery(id+"F0.wireOp",EDGE,"E1.sketch_text.stroke-125"),sQuery(id+"F0.wireOp",EDGE,"E1.sketch_text.stroke-126"),sQuery(id+"F0.wireOp",EDGE,"E1.sketch_text.stroke-127"),sQuery(id+"F0.wireOp",EDGE,"E1.sketch_text.stroke-128"),sQuery(id+"F0.wireOp",EDGE,"E1.sketch_text.stroke-129"),sQuery(id+"F0.wireOp",EDGE,"E1.sketch_text.stroke-130"),sQuery(id+"F0.wireOp",EDGE,"E1.sketch_text.stroke-131"),sQuery(id+"F0.wireOp",EDGE,"E1.sketch_text.stroke-139"),sQuery(id+"F0.wireOp",EDGE,"E1.sketch_text.stroke-140"),sQuery(id+"F0.wireOp",EDGE,"E1.sketch_text.stroke-141"),sQuery(id+"F0.wireOp",EDGE,"E1.sketch_text.stroke-142"),sQuery(id+"F0.wireOp",EDGE,"E1.sketch_text.stroke-143"),sQuery(id+"F0.wireOp",EDGE,"E1.sketch_text.stroke-144"),sQuery(id+"F0.wireOp",EDGE,"E1.sketch_text.stroke-145"),sQuery(id+"F0.wireOp",EDGE,"E1.sketch_text.stroke-146"),sQuery(id+"F0.wireOp",EDGE,"E1.sketch_text.stroke-147"),sQuery(id+"F0.wireOp",EDGE,"E1.sketch_text.stroke-148"),sQuery(id+"F0.wireOp",EDGE,"E1.sketch_text.stroke-149"),sQuery(id+"F0.wireOp",EDGE,"E1.sketch_text.stroke-150"),sQuery(id+"F0.wireOp",EDGE,"E1.sketch_text.stroke-151"),sQuery(id+"F0.wireOp",EDGE,"E1.sketch_text.stroke-152"),sQuery(id+"F0.wireOp",EDGE,"E1.sketch_text.stroke-153"),sQuery(id+"F0.wireOp",EDGE,"E1.sketch_text.stroke-154"),sQuery(id+"F0.wireOp",EDGE,"E1.sketch_text.stroke-155"),sQuery(id+"F0.wireOp",EDGE,"E1.sketch_text.stroke-156"),sQuery(id+"F0.wireOp",EDGE,"E1.sketch_text.stroke-157"),sQuery(id+"F0.wireOp",EDGE,"E1.sketch_text.stroke-166"),sQuery(id+"F0.wireOp",EDGE,"E1.sketch_text.stroke-167"),sQuery(id+"F0.wireOp",EDGE,"E1.sketch_text.stroke-168"),sQuery(id+"F0.wireOp",EDGE,"E1.sketch_text.stroke-169"),sQuery(id+"F0.wireOp",EDGE,"E1.sketch_text.stroke-170"),sQuery(id+"F0.wireOp",EDGE,"E1.sketch_text.stroke-171"),sQuery(id+"F0.wireOp",EDGE,"E1.sketch_text.stroke-172"),sQuery(id+"F0.wireOp",EDGE,"E1.sketch_text.stroke-173"),sQuery(id+"F0.wireOp",EDGE,"E1.sketch_text.stroke-174"),sQuery(id+"F0.wireOp",EDGE,"E1.sketch_text.stroke-175"),sQuery(id+"F0.wireOp",EDGE,"E1.sketch_text.stroke-176"),sQuery(id+"F0.wireOp",EDGE,"E1.sketch_text.stroke-177"),sQuery(id+"F0.wireOp",EDGE,"E1.sketch_text.stroke-178"),sQuery(id+"F0.wireOp",EDGE,"E1.sketch_text.stroke-179"),sQuery(id+"F0.wireOp",EDGE,"E1.sketch_text.stroke-180"),sQuery(id+"F0.wireOp",EDGE,"E1.sketch_text.stroke-181"),sQuery(id+"F0.wireOp",EDGE,"E1.sketch_text.stroke-191"),sQuery(id+"F0.wireOp",EDGE,"E1.sketch_text.stroke-192"),sQuery(id+"F0.wireOp",EDGE,"E1.sketch_text.stroke-193"),sQuery(id+"F0.wireOp",EDGE,"E1.sketch_text.stroke-194"),sQuery(id+"F0.wireOp",EDGE,"E1.sketch_text.stroke-195"),sQuery(id+"F0.wireOp",EDGE,"E1.sketch_text.stroke-196"),sQuery(id+"F0.wireOp",EDGE,"E1.sketch_text.stroke-197"),sQuery(id+"F0.wireOp",EDGE,"E1.sketch_text.stroke-198"),sQuery(id+"F0.wireOp",EDGE,"E1.sketch_text.stroke-199"),sQuery(id+"F0.wireOp",EDGE,"E1.sketch_text.stroke-200"),sQuery(id+"F0.wireOp",EDGE,"E1.sketch_text.stroke-201"),sQuery(id+"F0.wireOp",EDGE,"E1.sketch_text.stroke-202"),sQuery(id+"F0.wireOp",EDGE,"E1.sketch_text.stroke-203"),sQuery(id+"F0.wireOp",EDGE,"E1.sketch_text.stroke-204"),sQuery(id+"F0.wireOp",EDGE,"E1.sketch_text.stroke-205"),sQuery(id+"F0.wireOp",EDGE,"E1.sketch_text.stroke-206"),sQuery(id+"F0.wireOp",EDGE,"E1.sketch_text.stroke-207"),sQuery(id+"F0.wireOp",EDGE,"E1.sketch_text.stroke-208"),sQuery(id+"F0.wireOp",EDGE,"E1.sketch_text.stroke-209"),sQuery(id+"F0.wireOp",EDGE,"E3.sketch_text.stroke-0"),sQuery(id+"F0.wireOp",EDGE,"E3.sketch_text.stroke-1"),sQuery(id+"F0.wireOp",EDGE,"E3.sketch_text.stroke-2"),sQuery(id+"F0.wireOp",EDGE,"E3.sketch_text.stroke-3"),sQuery(id+"F0.wireOp",EDGE,"E3.sketch_text.stroke-4"),sQuery(id+"F0.wireOp",EDGE,"E3.sketch_text.stroke-5"),sQuery(id+"F0.wireOp",EDGE,"E3.sketch_text.stroke-6"),sQuery(id+"F0.wireOp",EDGE,"E3.sketch_text.stroke-7"),sQuery(id+"F0.wireOp",EDGE,"E3.sketch_text.stroke-8"),sQuery(id+"F0.wireOp",EDGE,"E3.sketch_text.stroke-9"),sQuery(id+"F0.wireOp",EDGE,"E3.sketch_text.stroke-10"),sQuery(id+"F0.wireOp",EDGE,"E3.sketch_text.stroke-11"),sQuery(id+"F0.wireOp",EDGE,"E3.sketch_text.stroke-12"),sQuery(id+"F0.wireOp",EDGE,"E3.sketch_text.stroke-13"),sQuery(id+"F0.wireOp",EDGE,"E3.sketch_text.stroke-14"),sQuery(id+"F0.wireOp",EDGE,"E3.sketch_text.stroke-24"),sQuery(id+"F0.wireOp",EDGE,"E3.sketch_text.stroke-25"),sQuery(id+"F0.wireOp",EDGE,"E3.sketch_text.stroke-26"),sQuery(id+"F0.wireOp",EDGE,"E3.sketch_text.stroke-27"),sQuery(id+"F0.wireOp",EDGE,"E3.sketch_text.stroke-28"),sQuery(id+"F0.wireOp",EDGE,"E3.sketch_text.stroke-29"),sQuery(id+"F0.wireOp",EDGE,"E3.sketch_text.stroke-30"),sQuery(id+"F0.wireOp",EDGE,"E3.sketch_text.stroke-31"),sQuery(id+"F0.wireOp",EDGE,"E3.sketch_text.stroke-32"),sQuery(id+"F0.wireOp",EDGE,"E3.sketch_text.stroke-33"),sQuery(id+"F0.wireOp",EDGE,"E3.sketch_text.stroke-34"),sQuery(id+"F0.wireOp",EDGE,"E3.sketch_text.stroke-35"),sQuery(id+"F0.wireOp",EDGE,"E3.sketch_text.stroke-36"),sQuery(id+"F0.wireOp",EDGE,"E3.sketch_text.stroke-37"),sQuery(id+"F0.wireOp",EDGE,"E3.sketch_text.stroke-43"),sQuery(id+"F0.wireOp",EDGE,"E3.sketch_text.stroke-44"),sQuery(id+"F0.wireOp",EDGE,"E3.sketch_text.stroke-45"),sQuery(id+"F0.wireOp",EDGE,"E3.sketch_text.stroke-46"),sQuery(id+"F0.wireOp",EDGE,"E3.sketch_text.stroke-47"),sQuery(id+"F0.wireOp",EDGE,"E3.sketch_text.stroke-48"),sQuery(id+"F0.wireOp",EDGE,"E3.sketch_text.stroke-49"),sQuery(id+"F0.wireOp",EDGE,"E3.sketch_text.stroke-50"),sQuery(id+"F0.wireOp",EDGE,"E3.sketch_text.stroke-51"),sQuery(id+"F0.wireOp",EDGE,"E3.sketch_text.stroke-52"),sQuery(id+"F0.wireOp",EDGE,"E3.sketch_text.stroke-53"),sQuery(id+"F0.wireOp",EDGE,"E3.sketch_text.stroke-54"),sQuery(id+"F0.wireOp",EDGE,"E3.sketch_text.stroke-55"),sQuery(id+"F0.wireOp",EDGE,"E3.sketch_text.stroke-56"),sQuery(id+"F0.wireOp",EDGE,"E3.sketch_text.stroke-57"),sQuery(id+"F0.wireOp",EDGE,"E3.sketch_text.stroke-58"),sQuery(id+"F0.wireOp",EDGE,"E3.sketch_text.stroke-59"),sQuery(id+"F0.wireOp",EDGE,"E3.sketch_text.stroke-60"),sQuery(id+"F0.wireOp",EDGE,"E3.sketch_text.stroke-61"),sQuery(id+"F0.wireOp",EDGE,"E3.sketch_text.stroke-62"),sQuery(id+"F0.wireOp",EDGE,"E3.sketch_text.stroke-63"),sQuery(id+"F0.wireOp",EDGE,"E3.sketch_text.stroke-64"),sQuery(id+"F0.wireOp",EDGE,"E3.sketch_text.stroke-65"),sQuery(id+"F0.wireOp",EDGE,"E3.sketch_text.stroke-74"),sQuery(id+"F0.wireOp",EDGE,"E3.sketch_text.stroke-75"),sQuery(id+"F0.wireOp",EDGE,"E3.sketch_text.stroke-76"),sQuery(id+"F0.wireOp",EDGE,"E3.sketch_text.stroke-77"),sQuery(id+"F0.wireOp",EDGE,"E3.sketch_text.stroke-78"),sQuery(id+"F0.wireOp",EDGE,"E3.sketch_text.stroke-79"),sQuery(id+"F0.wireOp",EDGE,"E3.sketch_text.stroke-80"),sQuery(id+"F0.wireOp",EDGE,"E3.sketch_text.stroke-81"),sQuery(id+"F0.wireOp",EDGE,"E3.sketch_text.stroke-82"),sQuery(id+"F0.wireOp",EDGE,"E3.sketch_text.stroke-83"),sQuery(id+"F0.wireOp",EDGE,"E3.sketch_text.stroke-84"),sQuery(id+"F0.wireOp",EDGE,"E3.sketch_text.stroke-85"),sQuery(id+"F0.wireOp",EDGE,"E3.sketch_text.stroke-86"),sQuery(id+"F0.wireOp",EDGE,"E3.sketch_text.stroke-87"),sQuery(id+"F0.wireOp",EDGE,"E3.sketch_text.stroke-88"),sQuery(id+"F0.wireOp",EDGE,"E3.sketch_text.stroke-89"),sQuery(id+"F0.wireOp",EDGE,"E3.sketch_text.stroke-90"),sQuery(id+"F0.wireOp",EDGE,"E3.sketch_text.stroke-91"),sQuery(id+"F0.wireOp",EDGE,"E3.sketch_text.stroke-92"),sQuery(id+"F0.wireOp",EDGE,"E3.sketch_text.stroke-93"),sQuery(id+"F0.wireOp",EDGE,"E3.sketch_text.stroke-94"),sQuery(id+"F0.wireOp",EDGE,"E3.sketch_text.stroke-95"),sQuery(id+"F0.wireOp",EDGE,"E3.sketch_text.stroke-96"),sQuery(id+"F0.wireOp",EDGE,"E3.sketch_text.stroke-97"),sQuery(id+"F0.wireOp",EDGE,"E3.sketch_text.stroke-98"),sQuery(id+"F0.wireOp",EDGE,"E3.sketch_text.stroke-99"),sQuery(id+"F0.wireOp",EDGE,"E3.sketch_text.stroke-100"),sQuery(id+"F0.wireOp",EDGE,"E3.sketch_text.stroke-101"),sQuery(id+"F0.wireOp",EDGE,"E3.sketch_text.stroke-102"),sQuery(id+"F0.wireOp",EDGE,"E3.sketch_text.stroke-103"),sQuery(id+"F0.wireOp",EDGE,"E3.sketch_text.stroke-104"),sQuery(id+"F0.wireOp",EDGE,"E3.sketch_text.stroke-105"),sQuery(id+"F0.wireOp",EDGE,"E3.sketch_text.stroke-106"),sQuery(id+"F0.wireOp",EDGE,"E3.sketch_text.stroke-107"),sQuery(id+"F0.wireOp",EDGE,"E3.sketch_text.stroke-108"),sQuery(id+"F0.wireOp",EDGE,"E3.sketch_text.stroke-109"),sQuery(id+"F0.wireOp",EDGE,"E3.sketch_text.stroke-110"),sQuery(id+"F0.wireOp",EDGE,"E3.sketch_text.stroke-111"),sQuery(id+"F0.wireOp",EDGE,"E3.sketch_text.stroke-112"),sQuery(id+"F0.wireOp",EDGE,"E3.sketch_text.stroke-121"),sQuery(id+"F0.wireOp",EDGE,"E3.sketch_text.stroke-122"),sQuery(id+"F0.wireOp",EDGE,"E3.sketch_text.stroke-123"),sQuery(id+"F0.wireOp",EDGE,"E3.sketch_text.stroke-124"),sQuery(id+"F0.wireOp",EDGE,"E3.sketch_text.stroke-125"),sQuery(id+"F0.wireOp",EDGE,"E3.sketch_text.stroke-126"),sQuery(id+"F0.wireOp",EDGE,"E3.sketch_text.stroke-127"),sQuery(id+"F0.wireOp",EDGE,"E3.sketch_text.stroke-128"),sQuery(id+"F0.wireOp",EDGE,"E3.sketch_text.stroke-129"),sQuery(id+"F0.wireOp",EDGE,"E3.sketch_text.stroke-130"),sQuery(id+"F0.wireOp",EDGE,"E3.sketch_text.stroke-131"),sQuery(id+"F0.wireOp",EDGE,"E3.sketch_text.stroke-132"),sQuery(id+"F0.wireOp",EDGE,"E3.sketch_text.stroke-133"),sQuery(id+"F0.wireOp",EDGE,"E3.sketch_text.stroke-134"),sQuery(id+"F0.wireOp",EDGE,"E3.sketch_text.stroke-135"),sQuery(id+"F0.wireOp",EDGE,"E3.sketch_text.stroke-136"),sQuery(id+"F0.wireOp",EDGE,"E3.sketch_text.stroke-137"),sQuery(id+"F0.wireOp",EDGE,"E3.sketch_text.stroke-138"),sQuery(id+"F0.wireOp",EDGE,"E3.sketch_text.stroke-139"),sQuery(id+"F0.wireOp",EDGE,"E3.sketch_text.stroke-140"),sQuery(id+"F0.wireOp",EDGE,"E3.sketch_text.stroke-141"),sQuery(id+"F0.wireOp",EDGE,"E3.sketch_text.stroke-142"),sQuery(id+"F0.wireOp",EDGE,"E3.sketch_text.stroke-143"),sQuery(id+"F0.wireOp",EDGE,"E3.sketch_text.stroke-152"),sQuery(id+"F0.wireOp",EDGE,"E3.sketch_text.stroke-153"),sQuery(id+"F0.wireOp",EDGE,"E3.sketch_text.stroke-154"),sQuery(id+"F0.wireOp",EDGE,"E3.sketch_text.stroke-155"),sQuery(id+"F0.wireOp",EDGE,"E3.sketch_text.stroke-156"),sQuery(id+"F0.wireOp",EDGE,"E3.sketch_text.stroke-157"),sQuery(id+"F0.wireOp",EDGE,"E3.sketch_text.stroke-158"),sQuery(id+"F0.wireOp",EDGE,"E3.sketch_text.stroke-159"),sQuery(id+"F0.wireOp",EDGE,"E3.sketch_text.stroke-160"),sQuery(id+"F0.wireOp",EDGE,"E3.sketch_text.stroke-161"),sQuery(id+"F0.wireOp",EDGE,"E3.sketch_text.stroke-162"),sQuery(id+"F0.wireOp",EDGE,"E3.sketch_text.stroke-163"),sQuery(id+"F0.wireOp",EDGE,"E3.sketch_text.stroke-164"),sQuery(id+"F0.wireOp",EDGE,"E3.sketch_text.stroke-165"),sQuery(id+"F0.wireOp",EDGE,"E3.sketch_text.stroke-166"),sQuery(id+"F0.wireOp",EDGE,"E3.sketch_text.stroke-167"),sQuery(id+"F0.wireOp",EDGE,"E3.sketch_text.stroke-168"),sQuery(id+"F0.wireOp",EDGE,"E3.sketch_text.stroke-169"),sQuery(id+"F0.wireOp",EDGE,"E3.sketch_text.stroke-170"),sQuery(id+"F0.wireOp",EDGE,"E3.sketch_text.stroke-171"),sQuery(id+"F0.wireOp",EDGE,"E3.sketch_text.stroke-172"),sQuery(id+"F0.wireOp",EDGE,"E3.sketch_text.stroke-173"),sQuery(id+"F0.wireOp",EDGE,"E3.sketch_text.stroke-174"),sQuery(id+"F0.wireOp",EDGE,"E3.sketch_text.stroke-175"),sQuery(id+"F0.wireOp",EDGE,"E3.sketch_text.stroke-176"),sQuery(id+"F0.wireOp",EDGE,"E3.sketch_text.stroke-177"),sQuery(id+"F0.wireOp",EDGE,"E3.sketch_text.stroke-178"),sQuery(id+"F0.wireOp",EDGE,"E3.sketch_text.stroke-179"),sQuery(id+"F0.wireOp",EDGE,"E3.sketch_text.stroke-180"),sQuery(id+"F0.wireOp",EDGE,"E3.sketch_text.stroke-181"),sQuery(id+"F0.wireOp",EDGE,"E3.sketch_text.stroke-182"),sQuery(id+"F0.wireOp",EDGE,"E3.sketch_text.stroke-183"),sQuery(id+"F0.wireOp",EDGE,"E3.sketch_text.stroke-184"),sQuery(id+"F0.wireOp",EDGE,"E3.sketch_text.stroke-185"),sQuery(id+"F0.wireOp",EDGE,"E3.sketch_text.stroke-186"),sQuery(id+"F0.wireOp",EDGE,"E3.sketch_text.stroke-187"),sQuery(id+"F0.wireOp",EDGE,"E3.sketch_text.stroke-188"),sQuery(id+"F0.wireOp",EDGE,"E3.sketch_text.stroke-189"),sQuery(id+"F0.wireOp",EDGE,"E3.sketch_text.stroke-195"),sQuery(id+"F0.wireOp",EDGE,"E3.sketch_text.stroke-196"),sQuery(id+"F0.wireOp",EDGE,"E3.sketch_text.stroke-197"),sQuery(id+"F0.wireOp",EDGE,"E3.sketch_text.stroke-198"),sQuery(id+"F0.wireOp",EDGE,"E3.sketch_text.stroke-199"),sQuery(id+"F0.wireOp",EDGE,"E3.sketch_text.stroke-200"),sQuery(id+"F0.wireOp",EDGE,"E3.sketch_text.stroke-201"),sQuery(id+"F0.wireOp",EDGE,"E3.sketch_text.stroke-202"),sQuery(id+"F0.wireOp",EDGE,"E3.sketch_text.stroke-203"),sQuery(id+"F0.wireOp",EDGE,"E3.sketch_text.stroke-204"),sQuery(id+"F0.wireOp",EDGE,"E3.sketch_text.stroke-205"),sQuery(id+"F0.wireOp",EDGE,"E3.sketch_text.stroke-206"),sQuery(id+"F0.wireOp",EDGE,"E3.sketch_text.stroke-207"),sQuery(id+"F0.wireOp",EDGE,"E3.sketch_text.stroke-208"),sQuery(id+"F0.wireOp",EDGE,"E3.sketch_text.stroke-209"),sQuery(id+"F0.wireOp",EDGE,"E3.sketch_text.stroke-210"),sQuery(id+"F0.wireOp",EDGE,"E3.sketch_text.stroke-211"),sQuery(id+"F0.wireOp",EDGE,"E3.sketch_text.stroke-212"),sQuery(id+"F0.wireOp",EDGE,"E3.sketch_text.stroke-213"),sQuery(id+"F0.wireOp",EDGE,"E3.sketch_text.stroke-214"),sQuery(id+"F0.wireOp",EDGE,"E3.sketch_text.stroke-215"),sQuery(id+"F0.wireOp",EDGE,"E3.sketch_text.stroke-216"),sQuery(id+"F0.wireOp",EDGE,"E3.sketch_text.stroke-217"),sQuery(id+"F0.wireOp",EDGE,"E3.sketch_text.stroke-218"),sQuery(id+"F0.wireOp",EDGE,"E3.sketch_text.stroke-219"),sQuery(id+"F0.wireOp",EDGE,"E3.sketch_text.stroke-220"),sQuery(id+"F0.wireOp",EDGE,"E3.sketch_text.stroke-221"),sQuery(id+"F0.wireOp",EDGE,"E3.sketch_text.stroke-222"),sQuery(id+"F0.wireOp",EDGE,"E3.sketch_text.stroke-223"),sQuery(id+"F0.wireOp",EDGE,"E3.sketch_text.stroke-224"),sQuery(id+"F0.wireOp",EDGE,"E3.sketch_text.stroke-225"),sQuery(id+"F0.wireOp",EDGE,"E3.sketch_text.stroke-226"),sQuery(id+"F0.wireOp",EDGE,"E3.sketch_text.stroke-227"),sQuery(id+"F0.wireOp",EDGE,"E3.sketch_text.stroke-228"),sQuery(id+"F0.wireOp",EDGE,"E3.sketch_text.stroke-229"),sQuery(id+"F0.wireOp",EDGE,"E3.sketch_text.stroke-230"),sQuery(id+"F0.wireOp",EDGE,"E3.sketch_text.stroke-231"),sQuery(id+"F0.wireOp",EDGE,"E3.sketch_text.stroke-232"),sQuery(id+"F0.wireOp",EDGE,"E3.sketch_text.stroke-233"),sQuery(id+"F0.wireOp",EDGE,"E3.sketch_text.stroke-234"),sQuery(id+"F0.wireOp",EDGE,"E3.sketch_text.stroke-235"),sQuery(id+"F0.wireOp",EDGE,"E3.sketch_text.stroke-236"),sQuery(id+"F0.wireOp",EDGE,"E3.sketch_text.stroke-237"),sQuery(id+"F0.wireOp",EDGE,"E3.sketch_text.stroke-238"),sQuery(id+"F0.wireOp",EDGE,"E3.sketch_text.stroke-239"),sQuery(id+"F0.wireOp",EDGE,"E3.sketch_text.stroke-240"),sQuery(id+"F0.wireOp",EDGE,"E4.bottom"),sQuery(id+"F0.wireOp",EDGE,"E4.top"),sQuery(id+"F0.wireOp",EDGE,"E4.right")])],"isStart":false});
            var sketch = newSketch(context, id + "F7", { "sketchPlane" : qUnion([Q0])});
            skText(sketch, "E10", { "text": "Joyeux anniversaire ! ", "fontName": "OpenSans-Bold.ttf"});
            const initialGuessF7  = {"E10": [-0.01461, -0.00112, 1, 0, 0.002]};
            skSetInitialGuess(sketch, initialGuessF7);
            skSolve(sketch);
        }
        {
            var Q0;
            Q0 = qSketchRegion(id + "F7", true);
            extrude(context, id + "F8", {"entities" : qUnion([Q0]), "operationType" : NewBodyOperationType.REMOVE, "oppositeDirection" : true, "depth" : 1 * mm});
        }
    });
